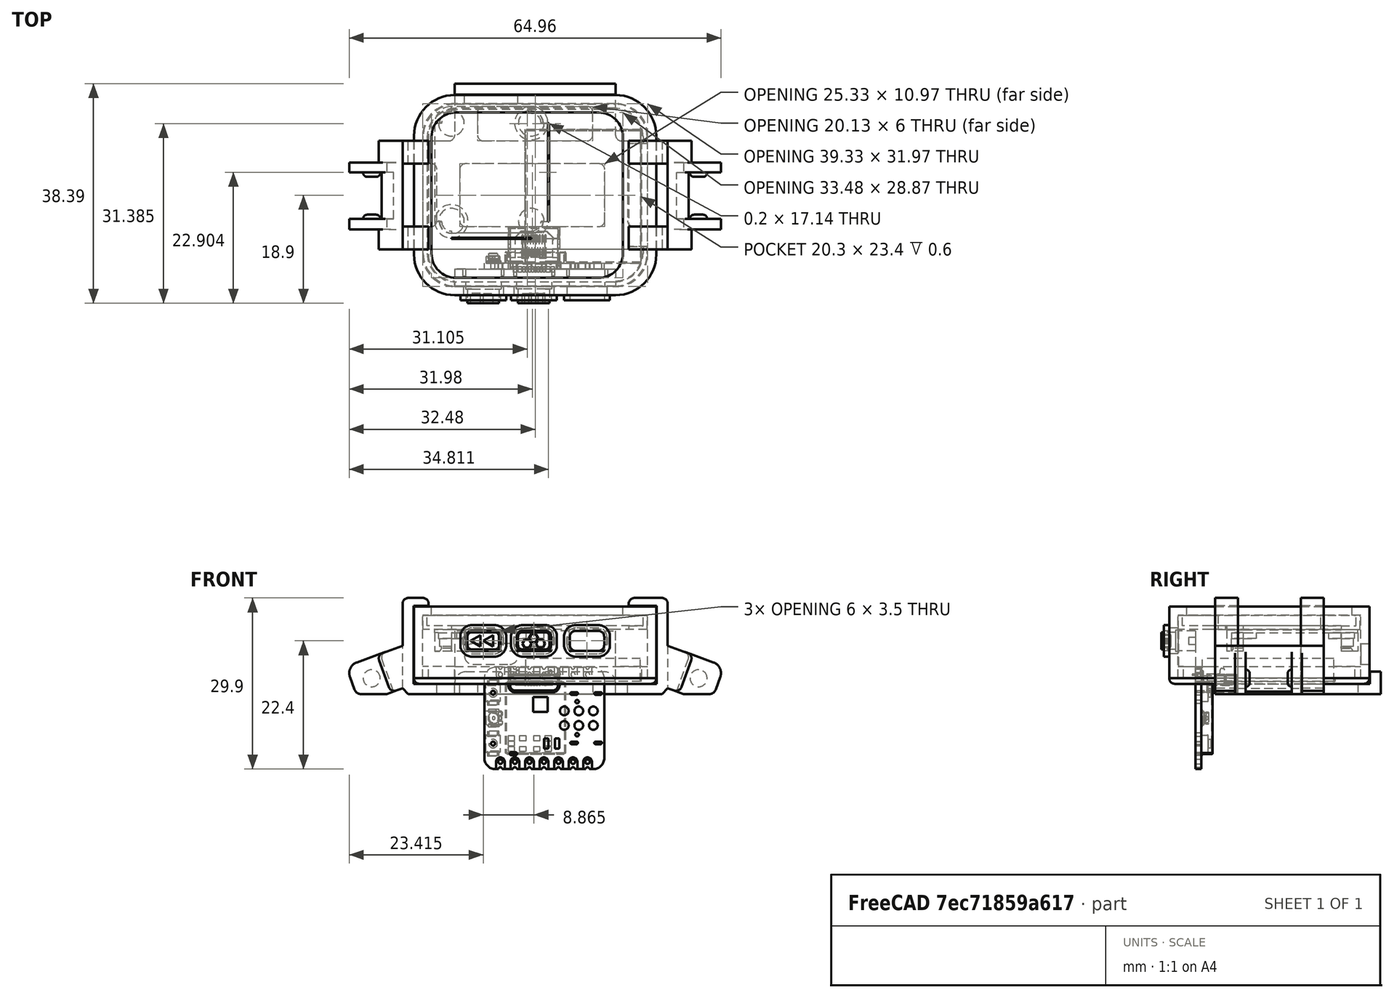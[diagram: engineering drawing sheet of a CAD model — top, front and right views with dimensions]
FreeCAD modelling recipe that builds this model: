
FCSTD DOCUMENT  (FreeCAD 1.0R39109 (Git))
Label: espwatch-final
License: All rights reserved
LicenseURL: https://en.wikipedia.org/wiki/All_rights_reserved
objects: Sketcher::SketchObject×41, Part::Feature×32, PartDesign::Pad×24, PartDesign::Pocket×17, PartDesign::Body×16, PartDesign::SubShapeBinder×15, PartDesign::Fillet×13, PartDesign::FeatureBase×8, App::Part×3, PartDesign::Thickness×2, PartDesign::Chamfer×2, Mesh::Feature×2, Part::Mirroring×1, Part::MultiFuse×1
note: 337 computed .brp shape members not serialized (recipe doc carries the construction recipe); baked Part::Feature solids carry a one-line shape summary decoded from their .brp

FEATURE [Sketcher::SketchObject] Sketch
  ArcFitTolerance = 1e-06
  AttachmentSupport = -> [XY_Plane]
  FullyConstrained = false
  MakeInternals = false
  MapMode = 5
  sketch-geometry (8):
    g0: LineSegment StartX=-15.185 StartY=13.865 StartZ=0 EndX=-15.185 EndY=-13.865 EndZ=0
    g1: LineSegment StartX=15.185 StartY=13.865 StartZ=0 EndX=15.185 EndY=-13.865 EndZ=0
    g2: LineSegment StartX=-10.185 StartY=18.865 StartZ=0 EndX=10.185 EndY=18.865 EndZ=0
    g3: LineSegment StartX=-10.185 StartY=-18.865 StartZ=0 EndX=10.185 EndY=-18.865 EndZ=0
    g4: ArcOfCircle CenterX=-10.185 CenterY=-13.865 CenterZ=0 NormalX=0 NormalY=0 NormalZ=1 AngleXU=0 Radius=5 StartAngle=3.14159 EndAngle=4.71239
    g5: ArcOfCircle CenterX=-10.185 CenterY=13.865 CenterZ=0 NormalX=0 NormalY=0 NormalZ=1 AngleXU=0 Radius=5.00002 StartAngle=1.5708 EndAngle=3.14159
    g6: ArcOfCircle CenterX=10.185 CenterY=13.865 CenterZ=0 NormalX=0 NormalY=0 NormalZ=1 AngleXU=0 Radius=5.00002 StartAngle=0 EndAngle=1.57079
    g7: ArcOfCircle CenterX=10.185 CenterY=-13.865 CenterZ=0 NormalX=0 NormalY=0 NormalZ=1 AngleXU=0 Radius=5.00002 StartAngle=4.71239 EndAngle=6.28318
  constraints (20):
    c: Vertical(g0)
    c: Vertical(g1)
    c: Horizontal(g2)
    c: Horizontal(g3)
    c: Coincident(g4,g0)
    c: Coincident(g4,g3)
    c: Coincident(g5,g2)
    c: Coincident(g5,g0)
    c: Coincident(g6,g2)
    c: Coincident(g6,g1)
    c: Coincident(g7,g1)
    c: Coincident(g7,g3)
    c: Equal(g0,g1)
    c: Equal(g3,g2)
    c: Radius(g4) = 5
    c: DistanceX(g0,g1) = 30.37
    c: DistanceY(g5,g6) = 0
    c: Equal(g5,g6)
    c: Equal(g7,g6)
    c: DistanceY(g3,g2) = 37.73
FEATURE [PartDesign::Pad] Pad
  Direction = (0,0,1)
  Length = 1.9
  Length2 = 10
  Profile = -> Sketch
  ReferenceAxis = -> Sketch [N_Axis]
  Refine = true
  Suppressed = false
  Type = 0
FEATURE [PartDesign::Thickness] Thickness
  Base = -> Pad [Face10]
  BaseFeature = -> Pad
  Intersection = false
  Join = 1
  Mode = 0
  Refine = true
  SupportTransform = false
  Suppressed = false
  Value = 0.7
FEATURE [Sketcher::SketchObject] Sketch001
  ArcFitTolerance = 1e-06
  AttachmentSupport = -> [XY_Plane]
  ExternalGeometry = -> [Thickness]
  FullyConstrained = true
  MakeInternals = false
  MapMode = 5
  sketch-geometry (4):
    g0: LineSegment StartX=-9 StartY=19.365 StartZ=0 EndX=-9 EndY=16.365 EndZ=0
    g1: LineSegment StartX=-9 StartY=16.365 StartZ=0 EndX=9 EndY=16.365 EndZ=0
    g2: LineSegment StartX=9 StartY=16.365 StartZ=0 EndX=9 EndY=19.365 EndZ=0
    g3: LineSegment StartX=9 StartY=19.365 StartZ=0 EndX=-9 EndY=19.365 EndZ=0
  constraints (12):
    c: Coincident(g0,g1)
    c: Coincident(g1,g2)
    c: Coincident(g2,g3)
    c: Coincident(g3,g0)
    c: Vertical(g0)
    c: Vertical(g2)
    c: Horizontal(g1)
    c: Horizontal(g3)
    c: DistanceY(g0,g0) = 3
    c: DistanceX(g3,g3) = 18
    c: DistanceY(g0,g-3) = -0.5
    c: DistanceX(g-1,g1) = 9
FEATURE [PartDesign::Pocket] Pocket
  BaseFeature = -> Thickness
  Direction = (0,0,-1)
  Length = 1
  Length2 = 5
  Profile = -> Sketch001
  ReferenceAxis = -> Sketch001 [N_Axis]
  Refine = true
  Reversed = true
  Suppressed = false
  Type = 4
FEATURE [Sketcher::SketchObject] Sketch002
  ArcFitTolerance = 1e-06
  AttachmentSupport = -> [XY_Plane]
  FullyConstrained = false
  MakeInternals = false
  MapMode = 5
  sketch-geometry (4):
    g0: LineSegment StartX=-25.2734 StartY=26.0356 StartZ=0 EndX=-25.2734 EndY=-23.7351 EndZ=0
    g1: LineSegment StartX=-25.2734 StartY=-23.7351 StartZ=0 EndX=24.3747 EndY=-23.7351 EndZ=0
    g2: LineSegment StartX=24.3747 StartY=-23.7351 StartZ=0 EndX=24.3747 EndY=26.0356 EndZ=0
    g3: LineSegment StartX=24.3747 StartY=26.0356 StartZ=0 EndX=-25.2734 EndY=26.0356 EndZ=0
  constraints (8):
    c: Coincident(g0,g1)
    c: Coincident(g1,g2)
    c: Coincident(g2,g3)
    c: Coincident(g3,g0)
    c: Vertical(g0)
    c: Vertical(g2)
    c: Horizontal(g1)
    c: Horizontal(g3)
FEATURE [PartDesign::Pocket] Pocket001
  BaseFeature = -> Pocket
  Direction = (0,0,-1)
  Length = 2
  Length2 = -0.6
  Profile = -> Sketch002
  ReferenceAxis = -> Sketch002 [N_Axis]
  Refine = true
  Suppressed = false
  Type = 4
FEATURE [Sketcher::SketchObject] Sketch003
  ArcFitTolerance = 1e-06
  AttachmentSupport = -> [XY_Plane001]
  FullyConstrained = true
  MakeInternals = false
  MapMode = 5
  sketch-geometry (4):
    g0: LineSegment StartX=20 StartY=23 StartZ=0 EndX=20 EndY=0 EndZ=0
    g1: LineSegment StartX=20 StartY=0 StartZ=0 EndX=0 EndY=0 EndZ=0
    g2: LineSegment StartX=0 StartY=0 StartZ=0 EndX=0 EndY=23 EndZ=0
    g3: LineSegment StartX=0 StartY=23 StartZ=0 EndX=20 EndY=23 EndZ=0
  constraints (11):
    c: Coincident(g0,g1)
    c: Coincident(g1,g2)
    c: Coincident(g2,g3)
    c: Coincident(g3,g0)
    c: Vertical(g0)
    c: Vertical(g2)
    c: Horizontal(g1)
    c: Horizontal(g3)
    c: Coincident(g1,g-1)
    c: DistanceY(g0,g0) = 23
    c: DistanceX(g3,g3) = 20
FEATURE [PartDesign::Pad] Pad001
  Direction = (0,0,1)
  Length = 4
  Length2 = 10
  Profile = -> Sketch003
  ReferenceAxis = -> Sketch003 [N_Axis]
  Refine = true
  Suppressed = false
  Type = 0
FEATURE [PartDesign::Body] Body001  label="battery"
  AllowCompound = false
  Group = -> [Sketch003,Pad001]
  Origin = -> Origin001
  Placement = pos=(-1.3,1.2,1.1) rot=(0,0,1;0rad)
  Tip = -> Pad001
FEATURE [Part::Feature] Part__Feature  label="BOSS-EXTRUDE14_8_"
  shape: bbox 0.6 x 1 x 0.3 mm, 6 faces (baked)
FEATURE [Part::Feature] Part__Feature001  label="BOSS-EXTRUDE7_4_"
  shape: bbox 0.3 x 3.784 x 0.75 mm, 6 faces (baked)
FEATURE [Part::Feature] Part__Feature002  label="BOSS-EXTRUDE7_3_"
  shape: bbox 0.3 x 3.784 x 0.75 mm, 6 faces (baked)
FEATURE [Part::Feature] Part__Feature003  label="BOSS-EXTRUDE14_4_"
  shape: bbox 0.3 x 1 x 0.3 mm, 6 faces (baked)
FEATURE [Part::Feature] Part__Feature004  label="BOSS-EXTRUDE14_2_"
  shape: bbox 0.6 x 1 x 0.3 mm, 6 faces (baked)
FEATURE [Part::Feature] Part__Feature005  label="BOSS-EXTRUDE14_11_"
  shape: bbox 0.3 x 1 x 0.3 mm, 6 faces (baked)
FEATURE [Part::Feature] Part__Feature006  label="BOSS-EXTRUDE7_7_"
  shape: bbox 0.3 x 3.784 x 0.75 mm, 6 faces (baked)
FEATURE [Part::Feature] Part__Feature007  label="BOSS-EXTRUDE14_9_"
  shape: bbox 0.3 x 1 x 0.3 mm, 6 faces (baked)
FEATURE [Part::Feature] Part__Feature008  label="BOSS-EXTRUDE14_3_"
  shape: bbox 0.3 x 1 x 0.3 mm, 6 faces (baked)
FEATURE [Part::Feature] Part__Feature009  label="BOSS-EXTRUDE14_7_"
  shape: bbox 0.6 x 1 x 0.3 mm, 6 faces (baked)
FEATURE [Part::Feature] Part__Feature010  label="MIRROR2"
  shape: bbox 6.7 x 4.6 x 0.7 mm, 26 faces (baked)
FEATURE [Part::Feature] Part__Feature011  label="BOSS-EXTRUDE14_5_"
  shape: bbox 0.3 x 1 x 0.3 mm, 6 faces (baked)
FEATURE [Part::Feature] Part__Feature012  label="BOSS-EXTRUDE14_12_"
  shape: bbox 0.3 x 1 x 0.3 mm, 6 faces (baked)
FEATURE [Part::Feature] Part__Feature013  label="BOSS-EXTRUDE7_8_"
  shape: bbox 0.3 x 3.784 x 0.75 mm, 6 faces (baked)
FEATURE [Part::Feature] Part__Feature014  label="BOSS-EXTRUDE7_1_"
  shape: bbox 0.3 x 3.784 x 0.75 mm, 6 faces (baked)
FEATURE [Part::Feature] Part__Feature015  label="BOSS-EXTRUDE14_10_"
  shape: bbox 0.3 x 1 x 0.3 mm, 6 faces (baked)
FEATURE [Part::Feature] Part__Feature016  label="BOSS-EXTRUDE7_9_"
  shape: bbox 0.3 x 3.784 x 0.75 mm, 6 faces (baked)
FEATURE [Part::Feature] Part__Feature017  label="BOSS-EXTRUDE14_6_"
  shape: bbox 0.6 x 1 x 0.3 mm, 6 faces (baked)
FEATURE [Part::Feature] Part__Feature018  label="CHAMFER9"
  shape: bbox 8.94 x 7.3 x 4.2 mm, 103 faces (baked)
FEATURE [Part::Feature] Part__Feature019  label="BOSS-EXTRUDE14_1_"
  shape: bbox 0.3 x 1 x 0.3 mm, 6 faces (baked)
FEATURE [Part::Feature] Part__Feature020  label="BOSS-EXTRUDE7_6_"
  shape: bbox 0.3 x 3.784 x 0.75 mm, 6 faces (baked)
FEATURE [Part::Feature] Part__Feature021  label="BOSS-EXTRUDE7_2_"
  shape: bbox 0.3 x 3.784 x 0.75 mm, 6 faces (baked)
FEATURE [Part::Feature] Part__Feature022  label="CUT-EXTRUDE5"
  shape: bbox 8.867 x 2 x 3.668 mm, 129 faces (baked)
FEATURE [Part::Feature] Part__Feature023  label="BOSS-EXTRUDE7_5_"
  shape: bbox 0.3 x 3.784 x 0.75 mm, 6 faces (baked)
FEATURE [App::Part] USB_TYPE_C_PORT__1_  label="USB TYPE C PORT (1)"
  Group = -> [Part__Feature,Part__Feature001,Part__Feature002,Part__Feature003,Part__Feature004,Part__Feature005,Part__Feature006,Part__Feature007,Part__Feature008,Part__Feature009,Part__Feature010,Part__Feature011,Part__Feature012,Part__Feature013,Part__Feature014,Part__Feature015,Part__Feature016,Part__Feature017,Part__Feature018,Part__Feature019,Part__Feature020,Part__Feature021,Part__Feature022,+1 more]
  Origin = -> Origin002
  Placement = pos=(0,0,-1e-16) rot=(0,0,1;0rad)
FEATURE [App::Part] USB_TYPE_C_PORT  label="USB TYPE C PORT"
  Group = -> [USB_TYPE_C_PORT__1_]
  Origin = -> Origin003
  Placement = pos=(6.48966,2.605,-6.1114) rot=(0.57735,0.57735,-0.57735;2.0944rad)
FEATURE [Part::Feature] Part__Feature024  label="U.FL Connector v1"
  Placement = pos=(-7.04101,1,-6.10146) rot=(0,-1,0;1.5708rad)
  shape: bbox 2.6 x 1.3 x 3 mm, 54 faces, 3 solids (baked)
FEATURE [Part::Feature] Part__Feature025  label="Button (1)"
  shape: bbox 2.5 x 1.7 x 4.303 mm, 19 faces (baked)
FEATURE [Part::Feature] Part__Feature026  label="Shield"
  shape: bbox 10.6 x 2.7 x 12.6 mm, 38 faces (baked)
FEATURE [Part::Feature] Part__Feature027  label="Button (1)001"
  Placement = pos=(-3.73e-13,1.1e-15,8.89) rot=(0,0,1;0rad)
  shape: bbox 2.5 x 1.7 x 4.303 mm, 19 faces (baked)
FEATURE [Part::Feature] Part__Feature028  label="SOLID"
  shape: bbox 20.96 x 1 x 17.78 mm, 358 faces (baked)
FEATURE [App::Part] Seeed_Studio_XIAO_ESP32_C3_v15  label="Seeed Studio XIAO-ESP32-C3 v15"
  Group = -> [USB_TYPE_C_PORT,Part__Feature024,Part__Feature025,Part__Feature026,Part__Feature027,Part__Feature028]
  Origin = -> Origin004
  Placement = pos=(-13.57,15.1,7.7) rot=(0.57735,0.57735,-0.57735;4.18879rad)
FEATURE [Sketcher::SketchObject] Sketch011
  ArcFitTolerance = 1e-06
  AttachmentSupport = -> [XY_Plane]
  ExternalGeometry = -> [Pocket001]
  FullyConstrained = true
  MakeInternals = false
  MapMode = 5
  sketch-geometry (4):
    g0: LineSegment StartX=-9 StartY=18.865 StartZ=0 EndX=9 EndY=18.865 EndZ=0
    g1: LineSegment StartX=9 StartY=18.865 StartZ=0 EndX=9 EndY=19.665 EndZ=0
    g2: LineSegment StartX=9 StartY=19.665 StartZ=0 EndX=-9 EndY=19.665 EndZ=0
    g3: LineSegment StartX=-9 StartY=19.665 StartZ=0 EndX=-9 EndY=18.865 EndZ=0
  constraints (11):
    c: Coincident(g0,g1)
    c: Coincident(g1,g2)
    c: Coincident(g2,g3)
    c: Coincident(g3,g0)
    c: Horizontal(g0)
    c: Horizontal(g2)
    c: Vertical(g1)
    c: Vertical(g3)
    c: Coincident(g0,g-3)
    c: DistanceX(g0,g-3) = 0
    c: DistanceY(g1,g1) = 0.8
FEATURE [PartDesign::Pocket] Pocket005
  BaseFeature = -> Pocket001
  Direction = (0,0,-1)
  Length = 5
  Length2 = 5
  Midplane = true
  Profile = -> Sketch011
  ReferenceAxis = -> Sketch011 [N_Axis]
  Refine = true
  Suppressed = false
  Type = 0
FEATURE [PartDesign::SubShapeBinder] Binder
  BindCopyOnChange = 0
  BindMode = 0
  ClaimChildren = false
  Context = -> Body002 [Binder.]
  Fuse = false
  MakeFace = true
  OffsetFill = false
  OffsetIntersection = false
  OffsetJoinType = 0
  OffsetOpenResult = false
  PartialLoad = false
  Refine = true
  Relative = true
  Support = -> [Body[Pocket005.,Pocket005.]]
  _Version = 2
FEATURE [Sketcher::SketchObject] Sketch012
  ArcFitTolerance = 1e-06
  AttachmentSupport = -> [XY_Plane005]
  FullyConstrained = true
  MakeInternals = false
  MapMode = 5
  sketch-geometry (10):
    g0: LineSegment StartX=-19.465 StartY=23.285 StartZ=0 EndX=-19.465 EndY=2.51502 EndZ=0
    g1: LineSegment StartX=-13.865 StartY=-3.085 StartZ=0 EndX=14.265 EndY=-3.085 EndZ=0
    g2: LineSegment StartX=19.865 StartY=2.51502 StartZ=0 EndX=19.865 EndY=23.285 EndZ=0
    g3: LineSegment StartX=14.265 StartY=28.885 StartZ=0 EndX=-13.865 EndY=28.885 EndZ=0
    g4: ArcOfCircle CenterX=-13.865 CenterY=23.285 CenterZ=0 NormalX=0 NormalY=0 NormalZ=1 AngleXU=0 Radius=5.60002 StartAngle=1.5708 EndAngle=3.14159
    g5: ArcOfCircle CenterX=-13.865 CenterY=2.51502 CenterZ=0 NormalX=0 NormalY=0 NormalZ=1 AngleXU=0 Radius=5.60002 StartAngle=3.14159 EndAngle=4.71239
    g6: ArcOfCircle CenterX=14.265 CenterY=2.51502 CenterZ=0 NormalX=0 NormalY=0 NormalZ=1 AngleXU=0 Radius=5.60002 StartAngle=4.71239 EndAngle=6.28319
    g7: ArcOfCircle CenterX=14.265 CenterY=23.285 CenterZ=0 NormalX=0 NormalY=0 NormalZ=1 AngleXU=0 Radius=5.60002 StartAngle=2e-16 EndAngle=1.5708
    g8: GeomPoint [constr] X=-19.465 Y=28.885 Z=0
    g9: GeomPoint [constr] X=19.865 Y=-3.085 Z=0
  constraints (24):
    c: Tangent(g0,g4) = -1.5708
    c: Tangent(g0,g5) = -1.5708
    c: Tangent(g1,g5) = -1.5708
    c: Tangent(g1,g6) = -1.5708
    c: Tangent(g2,g6) = -1.5708
    c: Tangent(g2,g7) = -1.5708
    c: Tangent(g3,g7) = -1.5708
    c: Tangent(g3,g4) = -1.5708
    c: Vertical(g0)
    c: Vertical(g2)
    c: Horizontal(g1)
    c: Horizontal(g3)
    c: Equal(g4,g5)
    c: Equal(g5,g6)
    c: Equal(g6,g7)
    c: PointOnObject(g8,g0)
    c: PointOnObject(g8,g3)
    c: PointOnObject(g9,g1)
    c: PointOnObject(g9,g2)
    c: Equal(g-5,g5)
    c: DistanceX(g0,g-7) = 0.2
    c: DistanceX(g-6,g2) = 0.2
    c: DistanceY(g-3,g3) = 0.2
    c: DistanceY(g1,g-4) = 0.2
FEATURE [PartDesign::Pad] Pad002
  Direction = (0,0,1)
  Length = 11
  Length2 = 10
  Profile = -> Sketch012
  ReferenceAxis = -> Sketch012 [N_Axis]
  Refine = true
  Suppressed = false
  Type = 0
FEATURE [PartDesign::Thickness] Thickness001
  Base = -> Pad002 [Face9]
  BaseFeature = -> Pad002
  Intersection = false
  Join = 1
  Mode = 0
  Refine = true
  SupportTransform = false
  Suppressed = false
  Value = 1.5
FEATURE [PartDesign::SubShapeBinder] Binder001
  BindCopyOnChange = 0
  BindMode = 0
  ClaimChildren = false
  Context = -> Body002 [Binder001.]
  Fuse = false
  MakeFace = true
  OffsetFill = false
  OffsetIntersection = false
  OffsetJoinType = 0
  OffsetOpenResult = false
  PartialLoad = false
  Refine = true
  Relative = true
  Support = -> [Body[Pocket005.Edge10,Pocket005.Edge21,Pocket005.Edge20,Pocket005.Edge23,Pocket005.Edge25,Pocket005.Edge7]]
  _Version = 2
FEATURE [Sketcher::SketchObject] Sketch013
  ArcFitTolerance = 1e-06
  AttachmentSupport = -> [XY_Plane005]
  ExternalGeometry = -> [Binder001]
  FullyConstrained = true
  MakeInternals = false
  MapMode = 5
  sketch-geometry (10):
    g0: LineSegment StartX=-13.665 StartY=-1.535 StartZ=0 EndX=11.315 EndY=-1.535 EndZ=0
    g1: LineSegment StartX=15.565 StartY=2.715 StartZ=0 EndX=15.565 EndY=23.085 EndZ=0
    g2: LineSegment StartX=11.315 StartY=27.335 StartZ=0 EndX=-13.665 EndY=27.335 EndZ=0
    g3: LineSegment StartX=-17.915 StartY=23.085 StartZ=0 EndX=-17.915 EndY=2.715 EndZ=0
    g4: ArcOfCircle CenterX=-13.665 CenterY=2.715 CenterZ=0 NormalX=0 NormalY=0 NormalZ=1 AngleXU=0 Radius=4.25 StartAngle=3.14159 EndAngle=4.71239
    g5: ArcOfCircle CenterX=11.315 CenterY=2.715 CenterZ=0 NormalX=0 NormalY=0 NormalZ=1 AngleXU=0 Radius=4.25 StartAngle=4.71239 EndAngle=6.28319
    g6: ArcOfCircle CenterX=11.315 CenterY=23.085 CenterZ=0 NormalX=0 NormalY=0 NormalZ=1 AngleXU=0 Radius=4.25 StartAngle=3e-16 EndAngle=1.5708
    g7: ArcOfCircle CenterX=-13.665 CenterY=23.085 CenterZ=0 NormalX=0 NormalY=0 NormalZ=1 AngleXU=0 Radius=4.25 StartAngle=1.5708 EndAngle=3.14159
    g8: GeomPoint [constr] X=-17.915 Y=-1.535 Z=0
    g9: GeomPoint [constr] X=15.565 Y=27.335 Z=0
  constraints (24):
    c: Tangent(g0,g4) = -1.5708
    c: Tangent(g0,g5) = -1.5708
    c: Tangent(g1,g5) = -1.5708
    c: Tangent(g1,g6) = -1.5708
    c: Tangent(g2,g6) = -1.5708
    c: Tangent(g2,g7) = -1.5708
    c: Tangent(g3,g7) = -1.5708
    c: Tangent(g3,g4) = -1.5708
    c: Horizontal(g0)
    c: Horizontal(g2)
    c: Vertical(g1)
    c: Vertical(g3)
    c: Equal(g4,g5)
    c: Equal(g5,g6)
    c: Equal(g6,g7)
    c: PointOnObject(g8,g0)
    c: PointOnObject(g8,g3)
    c: PointOnObject(g9,g1)
    c: PointOnObject(g9,g2)
    c: DistanceX(g-4,g3) = 0.75
    c: DistanceY(g-3,g0) = 0.75
    c: DistanceY(g2,g-6) = 0.75
    c: DistanceX(g1,g-7) = 3.5
    c: DistanceY(g3,g-6) = 0
FEATURE [PartDesign::Pocket] Pocket006
  BaseFeature = -> Thickness001
  Direction = (0,0,-1)
  Length = 20
  Length2 = 5
  Profile = -> Sketch013
  ReferenceAxis = -> Sketch013 [N_Axis]
  Refine = true
  Reversed = true
  Suppressed = false
  Type = 0
FEATURE [PartDesign::SubShapeBinder] Binder002
  BindCopyOnChange = 0
  BindMode = 0
  ClaimChildren = false
  Context = -> Body003 [Binder002.]
  Fuse = false
  MakeFace = true
  OffsetFill = false
  OffsetIntersection = false
  OffsetJoinType = 0
  OffsetOpenResult = false
  PartialLoad = false
  Refine = true
  Relative = true
  Support = -> [Seeed_Studio_XIAO_ESP32_C3_v15[Part__Feature028.Edge47,Part__Feature028.Edge45,Part__Feature028.Edge15,Part__Feature028.Edge13]]
  _Version = 2
FEATURE [Sketcher::SketchObject] Sketch015
  ArcFitTolerance = 1e-06
  AttachmentSupport = -> [XY_Plane006]
  ExternalGeometry = -> [Binder002]
  FullyConstrained = true
  MakeInternals = false
  MapMode = 5
  sketch-geometry (10):
    g0: LineSegment StartX=-14.4436 StartY=5.42666 StartZ=0 EndX=-0.473644 EndY=5.42666 EndZ=0
    g1: LineSegment StartX=2.4314 StartY=8.3317 StartZ=0 EndX=2.4314 EndY=25.4766 EndZ=0
    g2: LineSegment StartX=-0.473644 StartY=28.3817 StartZ=0 EndX=-14.4436 EndY=28.3817 EndZ=0
    g3: LineSegment StartX=-17.3486 StartY=25.4766 StartZ=0 EndX=-17.3486 EndY=8.3317 EndZ=0
    g4: ArcOfCircle CenterX=-14.4436 CenterY=8.3317 CenterZ=0 NormalX=0 NormalY=0 NormalZ=1 AngleXU=0 Radius=2.90504 StartAngle=3.14159 EndAngle=4.71239
    g5: ArcOfCircle CenterX=-0.473644 CenterY=8.3317 CenterZ=0 NormalX=0 NormalY=0 NormalZ=1 AngleXU=0 Radius=2.90504 StartAngle=4.71239 EndAngle=6.28319
    g6: ArcOfCircle CenterX=-0.473644 CenterY=25.4766 CenterZ=0 NormalX=0 NormalY=0 NormalZ=1 AngleXU=0 Radius=2.90504 StartAngle=0 EndAngle=1.5708
    g7: ArcOfCircle CenterX=-14.4436 CenterY=25.4766 CenterZ=0 NormalX=0 NormalY=0 NormalZ=1 AngleXU=0 Radius=2.90504 StartAngle=1.5708 EndAngle=3.14159
    g8: GeomPoint [constr] X=-17.3486 Y=5.42666 Z=0
    g9: GeomPoint [constr] X=2.4314 Y=28.3817 Z=0
  constraints (22):
    c: Tangent(g0,g4) = -1.5708
    c: Tangent(g0,g5) = -1.5708
    c: Tangent(g1,g5) = -1.5708
    c: Tangent(g1,g6) = -1.5708
    c: Tangent(g2,g6) = -1.5708
    c: Tangent(g2,g7) = -1.5708
    c: Tangent(g3,g7) = -1.5708
    c: Tangent(g3,g4) = -1.5708
    c: Horizontal(g0)
    c: Horizontal(g2)
    c: Vertical(g1)
    c: Vertical(g3)
    c: Equal(g4,g5)
    c: Equal(g5,g6)
    c: Equal(g6,g7)
    c: PointOnObject(g8,g0)
    c: PointOnObject(g8,g3)
    c: PointOnObject(g9,g1)
    c: PointOnObject(g9,g2)
    c: Coincident(g6,g-3)
    c: Coincident(g4,g-5)
    c: DistanceY(g0,g-6) = 1
FEATURE [PartDesign::Pad] Pad003
  Direction = (0,0,1)
  Length = 9.5
  Length2 = -9
  Profile = -> Sketch015
  ReferenceAxis = -> Sketch015 [N_Axis]
  Refine = true
  Suppressed = false
  Type = 4
FEATURE [Sketcher::SketchObject] Sketch014
  ArcFitTolerance = 1e-06
  AttachmentSupport = -> [XY_Plane006]
  ExternalGeometry = -> [Binder002,Pad003]
  FullyConstrained = true
  MakeInternals = false
  MapMode = 5
  sketch-geometry (16):
    g0: ArcOfCircle CenterX=-14.4436 CenterY=25.4766 CenterZ=0 NormalX=0 NormalY=0 NormalZ=1 AngleXU=0 Radius=2.90504 StartAngle=1.57081 EndAngle=3.14159
    g1: ArcOfCircle CenterX=-14.4436 CenterY=25.4766 CenterZ=0 NormalX=0 NormalY=0 NormalZ=1 AngleXU=0 Radius=2.10504 StartAngle=1.57082 EndAngle=3.14157
    g2: LineSegment StartX=-16.5486 StartY=25.4767 StartZ=0 EndX=-17.3486 EndY=25.4766 EndZ=0
    g3: LineSegment StartX=-14.4436 StartY=27.5817 StartZ=0 EndX=-14.4436 EndY=28.3817 EndZ=0
    g4: ArcOfCircle CenterX=-0.473644 CenterY=25.4766 CenterZ=0 NormalX=0 NormalY=0 NormalZ=1 AngleXU=0 Radius=2.90504 StartAngle=0 EndAngle=1.57078
    g5: ArcOfCircle CenterX=-14.4436 CenterY=8.3317 CenterZ=0 NormalX=0 NormalY=0 NormalZ=1 AngleXU=0 Radius=2.90504 StartAngle=3.14161 EndAngle=4.71239
    g6: ArcOfCircle CenterX=-0.473644 CenterY=8.3317 CenterZ=0 NormalX=0 NormalY=0 NormalZ=1 AngleXU=0 Radius=2.90504 StartAngle=4.71239 EndAngle=6.28319
    g7: ArcOfCircle CenterX=-14.4436 CenterY=8.3317 CenterZ=0 NormalX=0 NormalY=0 NormalZ=1 AngleXU=0 Radius=2.10504 StartAngle=3.14161 EndAngle=4.71239
    g8: ArcOfCircle CenterX=-0.473644 CenterY=8.3317 CenterZ=0 NormalX=0 NormalY=0 NormalZ=1 AngleXU=0 Radius=2.10504 StartAngle=4.71239 EndAngle=6.28319
    g9: ArcOfCircle CenterX=-0.473644 CenterY=25.4766 CenterZ=0 NormalX=0 NormalY=0 NormalZ=1 AngleXU=0 Radius=2.10504 StartAngle=0 EndAngle=1.57078
    g10: LineSegment StartX=-0.4736 StartY=28.3817 StartZ=0 EndX=-0.4736 EndY=27.5817 EndZ=0
    g11: LineSegment StartX=1.6314 StartY=25.4766 StartZ=0 EndX=2.4314 EndY=25.4766 EndZ=0
    g12: LineSegment StartX=-0.473644 StartY=6.22666 StartZ=0 EndX=-0.473644 EndY=5.42666 EndZ=0
    g13: LineSegment StartX=1.6314 StartY=8.3317 StartZ=0 EndX=2.4314 EndY=8.3317 EndZ=0
    g14: LineSegment StartX=-17.3486 StartY=8.33166 StartZ=0 EndX=-16.5486 EndY=8.33166 EndZ=0
    g15: LineSegment StartX=-14.4436 StartY=6.22666 StartZ=0 EndX=-14.4436 EndY=5.42666 EndZ=0
  constraints (45):
    c: Coincident(g0,g-10)
    c: Coincident(g0,g-10)
    c: Coincident(g1,g-10)
    c: DistanceY(g-5,g1) = 0
    c: DistanceX(g-5,g1) = 0
    c: DistanceY(g-5,g1) = 0.2
    c: Coincident(g3,g1)
    c: Coincident(g3,g0)
    c: Vertical(g3)
    c: Coincident(g2,g0)
    c: Coincident(g4,g-11)
    c: Coincident(g4,g-11)
    c: Coincident(g5,g-9)
    c: Coincident(g5,g-9)
    c: Coincident(g8,g6)
    c: Coincident(g9,g-11)
    c: DistanceX(g-7,g9) = 0.2
    c: Coincident(g10,g4)
    c: Coincident(g10,g9)
    c: DistanceX(g9,g-7) = 0
    c: Parallel(g10,g-2)
    c: Coincident(g9,g11)
    c: Coincident(g4,g11)
    c: Perpendicular(g-2,g11)
    c: Coincident(g12,g8)
    c: Coincident(g12,g6)
    c: Coincident(g13,g8)
    c: Coincident(g13,g6)
    c: Horizontal(g13)
    c: Parallel(g12,g-2)
    c: Coincident(g6,g-8)
    c: Coincident(g6,g-8)
    c: DistanceX(g-3,g8) = 0.2
    c: DistanceY(g6,g-8) = 0
    c: Coincident(g14,g5)
    c: Coincident(g14,g7)
    c: Coincident(g15,g7)
    c: Coincident(g15,g5)
    c: Vertical(g15)
    c: Perpendicular(g-2,g14)
    c: DistanceX(g7,g-4) = 0.2
    c: DistanceY(g7,g5) = 0
    c: DistanceX(g5,g7) = 0
    c: Coincident(g2,g1)
    c: DistanceY(g-4,g7) = 0
FEATURE [PartDesign::Pad] Pad004
  BaseFeature = -> Pad003
  Direction = (0,0,1)
  Length = 5.8
  Length2 = -9.4
  Profile = -> Sketch014
  ReferenceAxis = -> Sketch014 [N_Axis]
  Refine = true
  Suppressed = false
  Type = 4
FEATURE [Sketcher::SketchObject] Sketch016
  ArcFitTolerance = 1e-06
  AttachmentSupport = -> [XY_Plane006]
  ExternalGeometry = -> [Binder002]
  FullyConstrained = true
  MakeInternals = false
  MapMode = 5
  sketch-geometry (4):
    g0: Circle CenterX=-14.4436 CenterY=8.3317 CenterZ=0 NormalX=0 NormalY=0 NormalZ=1 AngleXU=0 Radius=2.25
    g1: Circle CenterX=-0.473644 CenterY=8.3317 CenterZ=0 NormalX=0 NormalY=0 NormalZ=1 AngleXU=0 Radius=2.25
    g2: Circle CenterX=-0.473644 CenterY=25.4766 CenterZ=0 NormalX=0 NormalY=0 NormalZ=1 AngleXU=0 Radius=2.25
    g3: Circle CenterX=-14.4436 CenterY=25.4766 CenterZ=0 NormalX=0 NormalY=0 NormalZ=1 AngleXU=0 Radius=2.25
  constraints (9):
    c: Coincident(g0,g-4)
    c: Coincident(g1,g-3)
    c: Coincident(g2,g-6)
    c: Coincident(g3,g-5)
    c: Equal(g3,g0)
    c: Equal(g0,g1)
    c: Equal(g1,g2)
    c: Radius(g-6) = 1.90504
    c: Diameter(g2) = 4.5
FEATURE [PartDesign::Pad] Pad005
  BaseFeature = -> Pad004
  Direction = (0,0,1)
  Length = 9.4
  Length2 = -8
  Profile = -> Sketch016
  ReferenceAxis = -> Sketch016 [N_Axis]
  Refine = true
  Suppressed = false
  Type = 4
FEATURE [PartDesign::SubShapeBinder] Binder003
  BindCopyOnChange = 0
  BindMode = 0
  ClaimChildren = false
  Context = -> Body003 [Binder003.]
  Fuse = false
  MakeFace = true
  OffsetFill = false
  OffsetIntersection = false
  OffsetJoinType = 0
  OffsetOpenResult = false
  PartialLoad = false
  Refine = true
  Relative = true
  Support = -> [Pad005[Edge7,Edge44,Edge14,Edge55,Edge72,Edge93,Edge89,Edge84]]
  _Version = 2
FEATURE [Sketcher::SketchObject] Sketch017
  ArcFitTolerance = 1e-06
  AttachmentSupport = -> [XY_Plane006]
  ExternalGeometry = -> [Binder003]
  FullyConstrained = true
  MakeInternals = false
  MapMode = 5
  sketch-geometry (16):
    g0: ArcOfCircle CenterX=-14.4436 CenterY=8.3317 CenterZ=0 NormalX=0 NormalY=0 NormalZ=1 AngleXU=0 Radius=2.90504 StartAngle=3.14161 EndAngle=4.71239
    g1: ArcOfCircle CenterX=-0.473644 CenterY=8.3317 CenterZ=0 NormalX=0 NormalY=0 NormalZ=1 AngleXU=0 Radius=2.90504 StartAngle=4.71239 EndAngle=6.28319
    g2: ArcOfCircle CenterX=-0.473644 CenterY=25.4766 CenterZ=0 NormalX=0 NormalY=0 NormalZ=1 AngleXU=0 Radius=2.90504 StartAngle=3e-16 EndAngle=1.57078
    g3: ArcOfCircle CenterX=-14.4436 CenterY=25.4766 CenterZ=0 NormalX=0 NormalY=0 NormalZ=1 AngleXU=0 Radius=2.90504 StartAngle=1.57081 EndAngle=3.14159
    g4: ArcOfCircle CenterX=-14.4436 CenterY=8.3317 CenterZ=0 NormalX=0 NormalY=0 NormalZ=1 AngleXU=0 Radius=1.70504 StartAngle=3.14162 EndAngle=4.71239
    g5: ArcOfCircle CenterX=-14.4436 CenterY=25.4766 CenterZ=0 NormalX=0 NormalY=0 NormalZ=1 AngleXU=0 Radius=1.70504 StartAngle=1.57082 EndAngle=3.14157
    g6: ArcOfCircle CenterX=-0.473644 CenterY=25.4766 CenterZ=0 NormalX=0 NormalY=0 NormalZ=1 AngleXU=0 Radius=1.70504 StartAngle=2e-16 EndAngle=1.57077
    g7: ArcOfCircle CenterX=-0.473644 CenterY=8.3317 CenterZ=0 NormalX=0 NormalY=0 NormalZ=1 AngleXU=0 Radius=1.70504 StartAngle=4.71239 EndAngle=6.28319
    g8: LineSegment StartX=-14.4436 StartY=28.3817 StartZ=0 EndX=-14.4436 EndY=27.1817 EndZ=0
    g9: LineSegment StartX=-16.1486 StartY=25.4767 StartZ=0 EndX=-17.3486 EndY=25.4766 EndZ=0
    g10: LineSegment StartX=2.4314 StartY=25.4766 StartZ=0 EndX=1.2314 EndY=25.4766 EndZ=0
    g11: LineSegment StartX=-0.4736 StartY=28.3817 StartZ=0 EndX=-0.4736 EndY=27.1817 EndZ=0
    g12: LineSegment StartX=-14.4436 StartY=5.42666 StartZ=0 EndX=-14.4436 EndY=6.62666 EndZ=0
    g13: LineSegment StartX=-17.3486 StartY=8.33166 StartZ=0 EndX=-16.1486 EndY=8.33166 EndZ=0
    g14: LineSegment StartX=-0.473644 StartY=5.42666 StartZ=0 EndX=-0.473644 EndY=6.62666 EndZ=0
    g15: LineSegment StartX=2.4314 StartY=8.3317 StartZ=0 EndX=1.2314 EndY=8.3317 EndZ=0
  constraints (44):
    c: Coincident(g0,g-5)
    c: Coincident(g1,g-10)
    c: Coincident(g2,g-9)
    c: Coincident(g3,g-7)
    c: Coincident(g4,g0)
    c: Coincident(g5,g3)
    c: Coincident(g6,g2)
    c: Coincident(g7,g1)
    c: DistanceY(g-6,g5) = 0
    c: Coincident(g3,g-7)
    c: DistanceX(g3,g-7) = 0
    c: Coincident(g8,g3)
    c: Vertical(g8)
    c: Coincident(g5,g8)
    c: DistanceY(g5,g-6) = 0.4
    c: Coincident(g2,g-8)
    c: DistanceY(g-8,g2) = 0
    c: Coincident(g10,g2)
    c: Horizontal(g10)
    c: Coincident(g11,g2)
    c: Vertical(g11)
    c: Coincident(g6,g11)
    c: Coincident(g6,g10)
    c: DistanceX(g6,g-9) = 0.4
    c: Coincident(g0,g-5)
    c: DistanceX(g0,g-5) = 0
    c: Coincident(g12,g0)
    c: Coincident(g13,g0)
    c: Horizontal(g13)
    c: Parallel(g12,g-2)
    c: Coincident(g4,g13)
    c: Coincident(g4,g12)
    c: DistanceY(g-4,g4) = 0.4
    c: Coincident(g1,g-10)
    c: DistanceX(g1,g-10) = 0
    c: Coincident(g14,g1)
    c: Vertical(g14)
    c: Coincident(g15,g1)
    c: Horizontal(g15)
    c: Coincident(g15,g7)
    c: Coincident(g7,g14)
    c: DistanceY(g-3,g7) = 0.4
    c: Coincident(g9,g3)
    c: Coincident(g5,g9)
FEATURE [PartDesign::Pad] Pad006
  BaseFeature = -> Pad005
  Direction = (0,0,1)
  Length = 6.6
  Length2 = -5.8
  Profile = -> Sketch017
  ReferenceAxis = -> Sketch017 [N_Axis]
  Refine = true
  Suppressed = false
  Type = 4
FEATURE [PartDesign::Chamfer] Chamfer
  Angle = 35
  Base = -> Pad006 [Edge95,Edge92,Edge97,Edge100]
  BaseFeature = -> Pad006
  ChamferType = 2
  FlipDirection = false
  Refine = true
  Size = 0.5
  Size2 = 1
  SupportTransform = false
  Suppressed = false
  UseAllEdges = false
FEATURE [PartDesign::SubShapeBinder] Binder004
  BindCopyOnChange = 0
  BindMode = 0
  ClaimChildren = false
  Context = -> Body002 [Binder004.]
  Fuse = false
  MakeFace = true
  OffsetFill = false
  OffsetIntersection = false
  OffsetJoinType = 0
  OffsetOpenResult = false
  PartialLoad = false
  Refine = true
  Relative = true
  Support = -> <blob elided: 513 chars, md5=d62ed6e8>
  _Version = 2
FEATURE [Sketcher::SketchObject] Sketch018
  ArcFitTolerance = 1e-06
  AttachmentSupport = -> [XZ_Plane005]
  ExternalGeometry = -> [Binder004]
  FullyConstrained = true
  MakeInternals = false
  MapMode = 5
  Placement = pos=(0,0,0) rot=(1,0,0;1.5708rad)
  sketch-geometry (10):
    g0: LineSegment StartX=-10.6786 StartY=2.39 StartZ=0 EndX=-4.2386 EndY=2.39 EndZ=0
    g1: LineSegment StartX=-2.7886 StartY=3.84 StartZ=0 EndX=-2.7886 EndY=4.55 EndZ=0
    g2: LineSegment StartX=-4.2386 StartY=6 StartZ=0 EndX=-10.6786 EndY=6 EndZ=0
    g3: LineSegment StartX=-12.1286 StartY=4.55 StartZ=0 EndX=-12.1286 EndY=3.84 EndZ=0
    g4: ArcOfCircle CenterX=-10.6786 CenterY=3.84 CenterZ=0 NormalX=0 NormalY=0 NormalZ=1 AngleXU=0 Radius=1.45 StartAngle=3.14159 EndAngle=4.71239
    g5: ArcOfCircle CenterX=-4.2386 CenterY=3.84 CenterZ=0 NormalX=0 NormalY=0 NormalZ=1 AngleXU=0 Radius=1.45 StartAngle=4.71239 EndAngle=6.28319
    g6: ArcOfCircle CenterX=-4.2386 CenterY=4.55 CenterZ=0 NormalX=0 NormalY=0 NormalZ=1 AngleXU=0 Radius=1.45 StartAngle=0 EndAngle=1.5708
    g7: ArcOfCircle CenterX=-10.6786 CenterY=4.55 CenterZ=0 NormalX=0 NormalY=0 NormalZ=1 AngleXU=0 Radius=1.45 StartAngle=1.5708 EndAngle=3.14159
    g8: GeomPoint [constr] X=-12.1286 Y=2.39 Z=0
    g9: GeomPoint [constr] X=-2.7886 Y=6 Z=0
  constraints (21):
    c: Tangent(g0,g4) = -1.5708
    c: Tangent(g0,g5) = -1.5708
    c: Tangent(g1,g5) = -1.5708
    c: Tangent(g1,g6) = -1.5708
    c: Tangent(g2,g6) = -1.5708
    c: Tangent(g2,g7) = -1.5708
    c: Tangent(g3,g7) = -1.5708
    c: Tangent(g3,g4) = -1.5708
    c: Horizontal(g0)
    c: Horizontal(g2)
    c: Vertical(g1)
    c: Vertical(g3)
    c: Equal(g5,g6)
    c: PointOnObject(g8,g0)
    c: PointOnObject(g8,g3)
    c: PointOnObject(g9,g1)
    c: PointOnObject(g9,g2)
    c: Coincident(g4,g-4)
    c: Coincident(g7,g-5)
    c: Coincident(g-8,g5)
    c: DistanceY(g0,g-8) = 0.2
FEATURE [PartDesign::Pocket] Pocket007
  BaseFeature = -> Pocket006
  Direction = (0,1,-2e-16)
  Length = 32
  Length2 = 5
  Profile = -> Sketch018
  ReferenceAxis = -> Sketch018 [N_Axis]
  Refine = true
  Suppressed = false
  Type = 0
FEATURE [PartDesign::SubShapeBinder] Binder005
  BindCopyOnChange = 0
  BindMode = 0
  ClaimChildren = false
  Context = -> Body004 [Binder005.]
  Fuse = false
  MakeFace = true
  OffsetFill = false
  OffsetIntersection = false
  OffsetJoinType = 0
  OffsetOpenResult = false
  PartialLoad = false
  Refine = true
  Relative = true
  Support = -> [Body002[Pocket007.Face4]]
  _Version = 2
FEATURE [Sketcher::SketchObject] Sketch019
  ArcFitTolerance = 1e-06
  AttachmentSupport = -> [XY_Plane007]
  ExternalGeometry = -> [Binder005]
  FullyConstrained = true
  MakeInternals = false
  MapMode = 5
  sketch-geometry (20):
    g0: LineSegment StartX=-13.865 StartY=-3.085 StartZ=0 EndX=14.265 EndY=-3.085 EndZ=0
    g1: LineSegment StartX=19.865 StartY=2.51502 StartZ=0 EndX=19.865 EndY=23.285 EndZ=0
    g2: LineSegment StartX=14.265 StartY=28.885 StartZ=0 EndX=-13.865 EndY=28.885 EndZ=0
    g3: LineSegment StartX=-19.465 StartY=23.285 StartZ=0 EndX=-19.465 EndY=2.51502 EndZ=0
    g4: ArcOfCircle CenterX=-13.865 CenterY=2.51502 CenterZ=0 NormalX=0 NormalY=0 NormalZ=1 AngleXU=0 Radius=5.60002 StartAngle=3.14159 EndAngle=4.71239
    g5: ArcOfCircle CenterX=14.265 CenterY=2.51502 CenterZ=0 NormalX=0 NormalY=0 NormalZ=1 AngleXU=0 Radius=5.60002 StartAngle=4.71239 EndAngle=6.28319
    g6: ArcOfCircle CenterX=14.265 CenterY=23.285 CenterZ=0 NormalX=0 NormalY=0 NormalZ=1 AngleXU=0 Radius=5.60002 StartAngle=0 EndAngle=1.5708
    g7: ArcOfCircle CenterX=-13.865 CenterY=23.285 CenterZ=0 NormalX=0 NormalY=0 NormalZ=1 AngleXU=0 Radius=5.60002 StartAngle=1.5708 EndAngle=3.14159
    g8: GeomPoint [constr] X=-19.465 Y=-3.085 Z=0
    g9: GeomPoint [constr] X=19.865 Y=28.885 Z=0
    g10: LineSegment StartX=-18.465 StartY=23.285 StartZ=0 EndX=-18.465 EndY=2.51502 EndZ=0
    g11: LineSegment StartX=-13.865 StartY=-2.085 StartZ=0 EndX=14.265 EndY=-2.085 EndZ=0
    g12: LineSegment StartX=18.865 StartY=2.51502 StartZ=0 EndX=18.865 EndY=23.285 EndZ=0
    g13: LineSegment StartX=14.265 StartY=27.885 StartZ=0 EndX=-13.865 EndY=27.885 EndZ=0
    g14: ArcOfCircle CenterX=-13.865 CenterY=23.285 CenterZ=0 NormalX=0 NormalY=0 NormalZ=1 AngleXU=0 Radius=4.60002 StartAngle=1.5708 EndAngle=3.14159
    g15: ArcOfCircle CenterX=-13.865 CenterY=2.51502 CenterZ=0 NormalX=0 NormalY=0 NormalZ=1 AngleXU=0 Radius=4.60002 StartAngle=3.14159 EndAngle=4.71239
    g16: ArcOfCircle CenterX=14.265 CenterY=2.51502 CenterZ=0 NormalX=0 NormalY=0 NormalZ=1 AngleXU=0 Radius=4.60002 StartAngle=4.71239 EndAngle=6.28319
    g17: ArcOfCircle CenterX=14.265 CenterY=23.285 CenterZ=0 NormalX=0 NormalY=0 NormalZ=1 AngleXU=0 Radius=4.60002 StartAngle=0 EndAngle=1.5708
    g18: GeomPoint [constr] X=-18.465 Y=27.885 Z=0
    g19: GeomPoint [constr] X=18.865 Y=-2.085 Z=0
  constraints (46):
    c: Tangent(g0,g4) = -1.5708
    c: Tangent(g0,g5) = -1.5708
    c: Tangent(g1,g5) = -1.5708
    c: Tangent(g1,g6) = -1.5708
    c: Tangent(g2,g6) = -1.5708
    c: Tangent(g2,g7) = -1.5708
    c: Tangent(g3,g7) = -1.5708
    c: Tangent(g3,g4) = -1.5708
    c: Horizontal(g0)
    c: Horizontal(g2)
    c: Vertical(g3)
    c: Equal(g6,g7)
    c: PointOnObject(g8,g0)
    c: PointOnObject(g8,g3)
    c: PointOnObject(g9,g1)
    c: PointOnObject(g9,g2)
    c: Coincident(g0,g-7)
    c: Coincident(g1,g-7)
    c: DistanceX(g-3,g0) = 0
    c: DistanceY(g3,g-6) = 0
    c: DistanceX(g-4,g2) = 0
    c: DistanceY(g3,g-6) = 0
    c: Tangent(g10,g14) = -1.5708
    c: Tangent(g10,g15) = -1.5708
    c: Tangent(g11,g15) = -1.5708
    c: Tangent(g11,g16) = -1.5708
    c: Tangent(g12,g16) = -1.5708
    c: Tangent(g12,g17) = -1.5708
    c: Tangent(g13,g17) = -1.5708
    c: Tangent(g13,g14) = -1.5708
    c: Vertical(g10)
    c: Vertical(g12)
    c: Horizontal(g11)
    c: Horizontal(g13)
    c: Equal(g14,g15)
    c: Equal(g15,g16)
    c: Equal(g16,g17)
    c: PointOnObject(g18,g10)
    c: PointOnObject(g18,g13)
    c: PointOnObject(g19,g11)
    c: PointOnObject(g19,g12)
    c: DistanceY(g13,g2) = 1
    c: DistanceX(g13,g2) = 0
    c: DistanceY(g1,g12) = 0
    c: DistanceY(g1,g12) = 0
    c: DistanceX(g0,g11) = 0
FEATURE [PartDesign::Pad] Pad007
  Direction = (0,0,1)
  Length = 2
  Length2 = 10
  Profile = -> Sketch019
  ReferenceAxis = -> Sketch019 [N_Axis]
  Refine = true
  Suppressed = false
  Type = 0
FEATURE [Sketcher::SketchObject] Sketch020
  ArcFitTolerance = 1e-06
  AttachmentSupport = -> [XY_Plane007]
  ExternalGeometry = -> [Binder005]
  FullyConstrained = true
  MakeInternals = false
  MapMode = 5
  sketch-geometry (10):
    g0: LineSegment StartX=-20.965 StartY=23.285 StartZ=0 EndX=-20.965 EndY=2.51502 EndZ=0
    g1: LineSegment StartX=-13.865 StartY=-4.585 StartZ=0 EndX=14.265 EndY=-4.585 EndZ=0
    g2: LineSegment StartX=21.365 StartY=2.51502 StartZ=0 EndX=21.365 EndY=23.285 EndZ=0
    g3: LineSegment StartX=14.265 StartY=30.385 StartZ=0 EndX=-13.865 EndY=30.385 EndZ=0
    g4: ArcOfCircle CenterX=-13.865 CenterY=23.285 CenterZ=0 NormalX=0 NormalY=0 NormalZ=1 AngleXU=0 Radius=7.10002 StartAngle=1.5708 EndAngle=3.14159
    g5: ArcOfCircle CenterX=-13.865 CenterY=2.51502 CenterZ=0 NormalX=0 NormalY=0 NormalZ=1 AngleXU=0 Radius=7.10002 StartAngle=3.14159 EndAngle=4.71239
    g6: ArcOfCircle CenterX=14.265 CenterY=2.51502 CenterZ=0 NormalX=0 NormalY=0 NormalZ=1 AngleXU=0 Radius=7.10002 StartAngle=4.71239 EndAngle=6.28319
    g7: ArcOfCircle CenterX=14.265 CenterY=23.285 CenterZ=0 NormalX=0 NormalY=0 NormalZ=1 AngleXU=0 Radius=7.10002 StartAngle=0 EndAngle=1.5708
    g8: GeomPoint [constr] X=-20.965 Y=30.385 Z=0
    g9: GeomPoint [constr] X=21.365 Y=-4.585 Z=0
  constraints (24):
    c: Tangent(g0,g4) = -1.5708
    c: Tangent(g0,g5) = -1.5708
    c: Tangent(g1,g5) = -1.5708
    c: Tangent(g1,g6) = -1.5708
    c: Tangent(g2,g6) = -1.5708
    c: Tangent(g2,g7) = -1.5708
    c: Tangent(g3,g7) = -1.5708
    c: Tangent(g3,g4) = -1.5708
    c: Vertical(g0)
    c: Vertical(g2)
    c: Horizontal(g1)
    c: Horizontal(g3)
    c: Equal(g4,g5)
    c: Equal(g5,g6)
    c: Equal(g6,g7)
    c: PointOnObject(g8,g0)
    c: PointOnObject(g8,g3)
    c: PointOnObject(g9,g1)
    c: PointOnObject(g9,g2)
    c: DistanceY(g-4,g3) = 0
    c: DistanceX(g-4,g3) = 0
    c: DistanceX(g3,g-3) = 0
    c: DistanceX(g-5,g2) = 0
    c: DistanceY(g1,g-6) = 0
FEATURE [PartDesign::Pad] Pad008
  BaseFeature = -> Pad007
  Direction = (0,0,1)
  Length = 1
  Length2 = 10
  Profile = -> Sketch020
  ReferenceAxis = -> Sketch020 [N_Axis]
  Refine = true
  Reversed = true
  Suppressed = false
  Type = 0
FEATURE [PartDesign::SubShapeBinder] Binder006
  BindCopyOnChange = 0
  BindMode = 0
  ClaimChildren = false
  Context = -> Body004 [Binder006.]
  Fuse = false
  MakeFace = true
  OffsetFill = false
  OffsetIntersection = false
  OffsetJoinType = 0
  OffsetOpenResult = false
  PartialLoad = false
  Refine = true
  Relative = true
  Support = -> [Body001[Pad001.Edge12,Pad001.Edge10,Pad001.Edge7,Pad001.Edge4]]
  _Version = 2
FEATURE [Sketcher::SketchObject] Sketch021
  ArcFitTolerance = 1e-06
  AttachmentSupport = -> [XY_Plane007]
  ExternalGeometry = -> [Binder006]
  FullyConstrained = true
  MakeInternals = false
  MapMode = 5
  sketch-geometry (4):
    g0: LineSegment StartX=-1.6 StartY=24.4 StartZ=0 EndX=-1.6 EndY=1 EndZ=0
    g1: LineSegment StartX=-1.6 StartY=1 StartZ=0 EndX=18.7 EndY=1 EndZ=0
    g2: LineSegment StartX=18.7 StartY=1 StartZ=0 EndX=18.7 EndY=24.4 EndZ=0
    g3: LineSegment StartX=18.7 StartY=24.4 StartZ=0 EndX=-1.6 EndY=24.4 EndZ=0
  constraints (12):
    c: Coincident(g0,g1)
    c: Coincident(g1,g2)
    c: Coincident(g2,g3)
    c: Coincident(g3,g0)
    c: Vertical(g0)
    c: Vertical(g2)
    c: Horizontal(g1)
    c: Horizontal(g3)
    c: DistanceY(g-3,g2) = 0.2
    c: DistanceX(g-3,g2) = 0
    c: DistanceX(g0,g-3) = 0.3
    c: DistanceY(g0,g-4) = 0.2
FEATURE [PartDesign::Pocket] Pocket008
  BaseFeature = -> Pad008
  Direction = (0,0,-1)
  Length = 0.6
  Length2 = 5
  Profile = -> Sketch021
  ReferenceAxis = -> Sketch021 [N_Axis]
  Refine = true
  Suppressed = false
  Type = 0
FEATURE [PartDesign::FeatureBase] Clone
  BaseFeature = -> Body001
  Placement = pos=(-1.3,1.2,1.1) rot=(0,0,1;0rad)
  Suppressed = false
FEATURE [PartDesign::Body] Body005  label="battery_clone"
  AllowCompound = false
  Group = -> [Clone]
  Origin = -> Origin008
  Placement = pos=(-0.1,0,-0.8) rot=(0,0,1;0rad)
  Tip = -> Clone
FEATURE [Sketcher::SketchObject] Sketch022
  ArcFitTolerance = 1e-06
  AttachmentSupport = -> [XZ_Plane005]
  ExternalGeometry = -> [Pocket007]
  FullyConstrained = true
  MakeInternals = false
  MapMode = 5
  Placement = pos=(0,0,0) rot=(1,0,0;1.5708rad)
  sketch-geometry (30):
    g0: LineSegment StartX=-11.865 StartY=7.25 StartZ=0 EndX=-11.865 EndY=5.75 EndZ=0
    g1: LineSegment StartX=-10.865 StartY=4.75 StartZ=0 EndX=-6.86497 EndY=4.75 EndZ=0
    g2: LineSegment StartX=-5.86497 StartY=5.75 StartZ=0 EndX=-5.86497 EndY=7.25 EndZ=0
    g3: LineSegment StartX=-6.86497 StartY=8.25 StartZ=0 EndX=-10.865 EndY=8.25 EndZ=0
    g4: ArcOfCircle CenterX=-10.865 CenterY=7.25 CenterZ=0 NormalX=0 NormalY=0 NormalZ=1 AngleXU=0 Radius=1 StartAngle=1.5708 EndAngle=3.14159
    g5: ArcOfCircle CenterX=-10.865 CenterY=5.75 CenterZ=0 NormalX=0 NormalY=0 NormalZ=1 AngleXU=0 Radius=1 StartAngle=3.14159 EndAngle=4.71239
    g6: ArcOfCircle CenterX=-6.86497 CenterY=5.75 CenterZ=0 NormalX=0 NormalY=0 NormalZ=1 AngleXU=0 Radius=1 StartAngle=4.71239 EndAngle=6.28319
    g7: ArcOfCircle CenterX=-6.86497 CenterY=7.25 CenterZ=0 NormalX=0 NormalY=0 NormalZ=1 AngleXU=0 Radius=1 StartAngle=0 EndAngle=1.5708
    g8: GeomPoint [constr] X=-11.865 Y=8.25 Z=0
    g9: GeomPoint [constr] X=-5.86497 Y=4.75 Z=0
    g10: LineSegment StartX=-3 StartY=7.25 StartZ=0 EndX=-3 EndY=5.75 EndZ=0
    g11: LineSegment StartX=-2 StartY=4.75 StartZ=0 EndX=2 EndY=4.75 EndZ=0
    g12: LineSegment StartX=3 StartY=5.75 StartZ=0 EndX=3 EndY=7.25 EndZ=0
    g13: LineSegment StartX=2 StartY=8.25 StartZ=0 EndX=-2 EndY=8.25 EndZ=0
    g14: ArcOfCircle CenterX=-2 CenterY=7.25 CenterZ=0 NormalX=0 NormalY=0 NormalZ=1 AngleXU=0 Radius=1 StartAngle=1.5708 EndAngle=3.14159
    g15: ArcOfCircle CenterX=-2 CenterY=5.75 CenterZ=0 NormalX=0 NormalY=0 NormalZ=1 AngleXU=0 Radius=1 StartAngle=3.14159 EndAngle=4.71239
    g16: ArcOfCircle CenterX=2 CenterY=5.75 CenterZ=0 NormalX=0 NormalY=0 NormalZ=1 AngleXU=0 Radius=1 StartAngle=4.71239 EndAngle=6.28319
    g17: ArcOfCircle CenterX=2 CenterY=7.25 CenterZ=0 NormalX=0 NormalY=0 NormalZ=1 AngleXU=0 Radius=1 StartAngle=1e-16 EndAngle=1.5708
    g18: GeomPoint [constr] X=-3 Y=8.25 Z=0
    g19: GeomPoint [constr] X=3 Y=4.75 Z=0
    g20: LineSegment StartX=6.265 StartY=7.25 StartZ=0 EndX=6.265 EndY=5.75 EndZ=0
    g21: LineSegment StartX=7.265 StartY=4.75 StartZ=0 EndX=11.265 EndY=4.75 EndZ=0
    g22: LineSegment StartX=12.265 StartY=5.75 StartZ=0 EndX=12.265 EndY=7.25 EndZ=0
    g23: LineSegment StartX=11.265 StartY=8.25 StartZ=0 EndX=7.265 EndY=8.25 EndZ=0
    g24: ArcOfCircle CenterX=7.265 CenterY=7.25 CenterZ=0 NormalX=0 NormalY=0 NormalZ=1 AngleXU=0 Radius=1 StartAngle=1.5708 EndAngle=3.14159
    g25: ArcOfCircle CenterX=7.265 CenterY=5.75 CenterZ=0 NormalX=0 NormalY=0 NormalZ=1 AngleXU=0 Radius=1 StartAngle=3.14159 EndAngle=4.71239
    g26: ArcOfCircle CenterX=11.265 CenterY=5.75 CenterZ=0 NormalX=0 NormalY=0 NormalZ=1 AngleXU=0 Radius=1 StartAngle=4.71239 EndAngle=6.28319
    g27: ArcOfCircle CenterX=11.265 CenterY=7.25 CenterZ=0 NormalX=0 NormalY=0 NormalZ=1 AngleXU=0 Radius=1 StartAngle=8e-16 EndAngle=1.5708
    g28: GeomPoint [constr] X=6.265 Y=8.25 Z=0
    g29: GeomPoint [constr] X=12.265 Y=4.75 Z=0
  constraints (72):
    c: Tangent(g0,g4) = -1.5708
    c: Tangent(g0,g5) = -1.5708
    c: Tangent(g1,g5) = -1.5708
    c: Tangent(g1,g6) = -1.5708
    c: Tangent(g2,g6) = -1.5708
    c: Tangent(g2,g7) = -1.5708
    c: Tangent(g3,g7) = -1.5708
    c: Tangent(g3,g4) = -1.5708
    c: Vertical(g0)
    c: Vertical(g2)
    c: Horizontal(g1)
    c: Horizontal(g3)
    c: Equal(g4,g5)
    c: Equal(g5,g6)
    c: Equal(g6,g7)
    c: PointOnObject(g8,g0)
    c: PointOnObject(g8,g3)
    c: PointOnObject(g9,g1)
    c: PointOnObject(g9,g2)
    c: Tangent(g10,g14) = -1.5708
    c: Tangent(g10,g15) = -1.5708
    c: Tangent(g11,g15) = -1.5708
    c: Tangent(g11,g16) = -1.5708
    c: Tangent(g12,g16) = -1.5708
    c: Tangent(g12,g17) = -1.5708
    c: Tangent(g13,g17) = -1.5708
    c: Tangent(g13,g14) = -1.5708
    c: Vertical(g10)
    c: Vertical(g12)
    c: Horizontal(g11)
    c: Horizontal(g13)
    c: Equal(g14,g15)
    c: Equal(g15,g16)
    c: Equal(g16,g17)
    c: PointOnObject(g18,g10)
    c: PointOnObject(g18,g13)
    c: PointOnObject(g19,g11)
    c: PointOnObject(g19,g12)
    c: Radius(g15) = 1
    c: Tangent(g20,g24) = -1.5708
    c: Tangent(g20,g25) = -1.5708
    c: Tangent(g21,g25) = -1.5708
    c: Tangent(g21,g26) = -1.5708
    c: Tangent(g22,g26) = -1.5708
    c: Tangent(g22,g27) = -1.5708
    c: Tangent(g23,g27) = -1.5708
    c: Tangent(g23,g24) = -1.5708
    c: Vertical(g20)
    c: Vertical(g22)
    c: Horizontal(g21)
    c: Horizontal(g23)
    c: Equal(g24,g25)
    c: Equal(g25,g26)
    c: Equal(g26,g27)
    c: PointOnObject(g28,g20)
    c: PointOnObject(g28,g23)
    c: PointOnObject(g29,g21)
    c: PointOnObject(g29,g22)
    c: Radius(g25) = 1
    c: Equal(g23,g13)
    c: Equal(g13,g3)
    c: Equal(g2,g12)
    c: Equal(g12,g22)
    c: DistanceY(g11,g13) = 3.5
    c: DistanceX(g10,g12) = 6
    c: Radius(g5) = 1
    c: DistanceY(g23,g13) = 0
    c: DistanceY(g13,g3) = 0
    c: DistanceX(g-1,g12) = 3
    c: DistanceX(g22,g-5) = 2
    c: DistanceX(g-3,g0) = 2
    c: DistanceY(g-1,g21) = 4.75
FEATURE [PartDesign::Pocket] Pocket009
  BaseFeature = -> Pocket007
  Direction = (0,1,-2e-16)
  Length = 5
  Length2 = 5
  Profile = -> Sketch022
  ReferenceAxis = -> Sketch022 [N_Axis]
  Refine = true
  Reversed = true
  Suppressed = false
  Type = 0
FEATURE [PartDesign::SubShapeBinder] Binder007
  BindCopyOnChange = 0
  BindMode = 0
  ClaimChildren = false
  Context = -> Body004 [Binder007.]
  Fuse = false
  MakeFace = true
  OffsetFill = false
  OffsetIntersection = false
  OffsetJoinType = 0
  OffsetOpenResult = false
  PartialLoad = false
  Refine = true
  Relative = true
  Support = -> [Body002[Pocket009.Edge113,Pocket009.Edge109,Pocket009.Edge111,Pocket009.Edge115,Pocket009.Edge103,Pocket009.Edge105,Pocket009.Edge101,Pocket009.Edge107]]
  _Version = 2
FEATURE [Sketcher::SketchObject] Sketch023
  ArcFitTolerance = 1e-06
  AttachmentSupport = -> [XZ_Plane007]
  ExternalGeometry = -> [Pocket008,Binder007]
  FullyConstrained = true
  MakeInternals = false
  MapMode = 5
  Placement = pos=(0,0,0) rot=(1,0,0;1.5708rad)
  sketch-geometry (16):
    g0: LineSegment StartX=-13.865 StartY=0 StartZ=0 EndX=14.265 EndY=0 EndZ=0
    g1: LineSegment StartX=14.265 StartY=0 StartZ=0 EndX=14.265 EndY=8.25 EndZ=0
    g2: LineSegment StartX=-13.865 StartY=8.25 StartZ=0 EndX=-13.865 EndY=0 EndZ=0
    g3: LineSegment StartX=-11.965 StartY=8.25 StartZ=0 EndX=-11.965 EndY=4.75 EndZ=0
    g4: LineSegment StartX=-11.965 StartY=4.75 StartZ=0 EndX=-5.76497 EndY=4.75 EndZ=0
    g5: LineSegment StartX=-5.76497 StartY=4.75 StartZ=0 EndX=-5.76497 EndY=8.25 EndZ=0
    g6: LineSegment StartX=-3.1 StartY=4.75 StartZ=0 EndX=3.1 EndY=4.75 EndZ=0
    g7: LineSegment StartX=3.1 StartY=4.75 StartZ=0 EndX=3.1 EndY=8.25 EndZ=0
    g8: LineSegment StartX=-3.1 StartY=8.25 StartZ=0 EndX=-3.1 EndY=4.75 EndZ=0
    g9: LineSegment StartX=6.165 StartY=4.75 StartZ=0 EndX=12.365 EndY=4.75 EndZ=0
    g10: LineSegment StartX=12.365 StartY=4.75 StartZ=0 EndX=12.365 EndY=8.25 EndZ=0
    g11: LineSegment StartX=6.165 StartY=8.25 StartZ=0 EndX=6.165 EndY=4.75 EndZ=0
    g12: LineSegment StartX=12.365 StartY=8.25 StartZ=0 EndX=14.265 EndY=8.25 EndZ=0
    g13: LineSegment StartX=-11.965 StartY=8.25 StartZ=0 EndX=-13.865 EndY=8.25 EndZ=0
    g14: LineSegment StartX=-5.76497 StartY=8.25 StartZ=0 EndX=-3.1 EndY=8.25 EndZ=0
    g15: LineSegment StartX=6.165 StartY=8.25 StartZ=0 EndX=3.1 EndY=8.25 EndZ=0
  constraints (47):
    c: Coincident(g0,g1)
    c: Coincident(g2,g0)
    c: Horizontal(g0)
    c: Vertical(g1)
    c: Vertical(g2)
    c: Coincident(g0,g-3)
    c: DistanceX(g0,g-3) = 0
    c: Coincident(g3,g4)
    c: Coincident(g4,g5)
    c: Vertical(g3)
    c: Vertical(g5)
    c: Horizontal(g4)
    c: Coincident(g6,g7)
    c: Coincident(g8,g6)
    c: Horizontal(g6)
    c: Vertical(g7)
    c: Vertical(g8)
    c: Coincident(g9,g10)
    c: Coincident(g11,g9)
    c: Horizontal(g9)
    c: Vertical(g10)
    c: Vertical(g11)
    c: DistanceX(g3,g5) = 6.2
    c: DistanceY(g5,g5) = 3.5
    c: Equal(g5,g7)
    c: Equal(g7,g10)
    c: DistanceX(g9,g-13) = 0.1
    c: DistanceX(g6,g-10) = 0.1
    c: DistanceX(g3,g-7) = 0.1
    c: DistanceY(g7,g-5) = 0
    c: Coincident(g12,g10)
    c: Coincident(g12,g1)
    c: Parallel(g12,g-1)
    c: Coincident(g13,g3)
    c: Coincident(g13,g2)
    c: Parallel(g13,g-1)
    c: Coincident(g14,g5)
    c: Coincident(g14,g8)
    c: Coincident(g15,g11)
    c: Coincident(g15,g7)
    c: Parallel(g15,g14)
    c: Parallel(g14,g13)
    c: DistanceY(g7,g8) = 0
    c: DistanceY(g10,g3) = 0
    c: DistanceY(g9,g6) = 0
    c: DistanceX(g-12,g6) = 0.1
    c: DistanceX(g-15,g9) = 0.1
FEATURE [PartDesign::Pad] Pad009
  BaseFeature = -> Pocket008
  Direction = (0,-1,2e-16)
  Length = 3
  Length2 = 10
  Profile = -> Sketch023
  ReferenceAxis = -> Sketch023 [N_Axis]
  Refine = true
  Suppressed = false
  Type = 0
FEATURE [Sketcher::SketchObject] Sketch024
  ArcFitTolerance = 1e-06
  AttachmentSupport = -> [XZ_Plane007]
  ExternalGeometry = -> [Pad009]
  FullyConstrained = true
  MakeInternals = false
  MapMode = 5
  Placement = pos=(0,0,0) rot=(1,0,0;1.5708rad)
  sketch-geometry (12):
    g0: LineSegment StartX=-12.465 StartY=7.1 StartZ=0 EndX=-12.465 EndY=5.9 EndZ=0
    g1: LineSegment StartX=-12.465 StartY=5.9 StartZ=0 EndX=-5.26497 EndY=5.9 EndZ=0
    g2: LineSegment StartX=-5.26497 StartY=5.9 StartZ=0 EndX=-5.26497 EndY=7.1 EndZ=0
    g3: LineSegment StartX=-5.26497 StartY=7.1 StartZ=0 EndX=-12.465 EndY=7.1 EndZ=0
    g4: LineSegment StartX=-3.6 StartY=5.9 StartZ=0 EndX=3.6 EndY=5.9 EndZ=0
    g5: LineSegment StartX=3.6 StartY=5.9 StartZ=0 EndX=3.6 EndY=7.1 EndZ=0
    g6: LineSegment StartX=3.6 StartY=7.1 StartZ=0 EndX=-3.6 EndY=7.1 EndZ=0
    g7: LineSegment StartX=-3.6 StartY=7.1 StartZ=0 EndX=-3.6 EndY=5.9 EndZ=0
    g8: LineSegment StartX=5.665 StartY=7.1 StartZ=0 EndX=5.665 EndY=5.9 EndZ=0
    g9: LineSegment StartX=5.665 StartY=5.9 StartZ=0 EndX=12.865 EndY=5.9 EndZ=0
    g10: LineSegment StartX=12.865 StartY=5.9 StartZ=0 EndX=12.865 EndY=7.1 EndZ=0
    g11: LineSegment StartX=12.865 StartY=7.1 StartZ=0 EndX=5.665 EndY=7.1 EndZ=0
  constraints (36):
    c: Coincident(g0,g1)
    c: Coincident(g1,g2)
    c: Coincident(g2,g3)
    c: Coincident(g3,g0)
    c: Vertical(g0)
    c: Vertical(g2)
    c: Horizontal(g1)
    c: Horizontal(g3)
    c: Coincident(g4,g5)
    c: Coincident(g5,g6)
    c: Coincident(g6,g7)
    c: Coincident(g7,g4)
    c: Horizontal(g4)
    c: Horizontal(g6)
    c: Vertical(g5)
    c: Vertical(g7)
    c: Coincident(g8,g9)
    c: Coincident(g9,g10)
    c: Coincident(g10,g11)
    c: Coincident(g11,g8)
    c: Vertical(g8)
    c: Vertical(g10)
    c: Horizontal(g9)
    c: Horizontal(g11)
    c: DistanceY(g8,g5) = 0
    c: DistanceY(g2,g6) = 0
    c: Equal(g2,g7)
    c: Equal(g5,g8)
    c: DistanceY(g8,g8) = 1.2
    c: DistanceX(g-3,g1) = 0.5
    c: DistanceX(g0,g-4) = 0.5
    c: DistanceX(g6,g-8) = 0.5
    c: DistanceX(g-5,g5) = 0.5
    c: DistanceX(g8,g-6) = 0.5
    c: DistanceX(g-7,g10) = 0.5
    c: DistanceY(g2,g-3) = 1.15
FEATURE [PartDesign::Pocket] Pocket010
  BaseFeature = -> Pad009
  Direction = (0,1,-2e-16)
  Length = 1.2
  Length2 = 5
  Profile = -> Sketch024
  ReferenceAxis = -> Sketch024 [N_Axis]
  Refine = true
  Reversed = true
  Suppressed = false
  Type = 0
FEATURE [PartDesign::SubShapeBinder] Binder008
  BindCopyOnChange = 0
  BindMode = 0
  ClaimChildren = false
  Context = -> Body006 [Binder008.]
  Fuse = false
  MakeFace = true
  OffsetFill = false
  OffsetIntersection = false
  OffsetJoinType = 0
  OffsetOpenResult = false
  PartialLoad = false
  Refine = true
  Relative = true
  Support = -> [Body002[Pocket011.Edge68,Pocket011.Edge64,Pocket011.Edge52,Pocket011.Edge48,Pocket011.Edge51,Pocket011.Edge54,Pocket011.Edge50,Pocket011.Edge66]]
  _Version = 2
FEATURE [PartDesign::SubShapeBinder] Binder009
  BindCopyOnChange = 0
  BindMode = 0
  ClaimChildren = false
  Context = -> Body006 [Binder009.]
  Fuse = false
  MakeFace = true
  OffsetFill = false
  OffsetIntersection = false
  OffsetJoinType = 0
  OffsetOpenResult = false
  PartialLoad = false
  Refine = true
  Relative = true
  Support = -> [Body002[Pocket011.Edge105,Pocket011.Edge101,Pocket011.Edge93,Pocket011.Edge97,Pocket011.Edge99,Pocket011.Edge95,Pocket011.Edge115,Pocket011.Edge114]]
  _Version = 2
FEATURE [Sketcher::SketchObject] Sketch026
  ArcFitTolerance = 1e-06
  AttachmentSupport = -> [XZ_Plane009]
  ExternalGeometry = -> [Binder008]
  FullyConstrained = true
  MakeInternals = false
  MapMode = 5
  Placement = pos=(0,0,0) rot=(1,0,0;1.5708rad)
  sketch-geometry (10):
    g0: LineSegment StartX=6.165 StartY=8.15 StartZ=0 EndX=6.165 EndY=6.65 EndZ=0
    g1: LineSegment StartX=7.265 StartY=5.55 StartZ=0 EndX=11.265 EndY=5.55 EndZ=0
    g2: LineSegment StartX=12.365 StartY=6.65 StartZ=0 EndX=12.365 EndY=8.15 EndZ=0
    g3: LineSegment StartX=11.265 StartY=9.25 StartZ=0 EndX=7.265 EndY=9.25 EndZ=0
    g4: ArcOfCircle CenterX=7.265 CenterY=8.15 CenterZ=0 NormalX=0 NormalY=0 NormalZ=1 AngleXU=0 Radius=1.1 StartAngle=1.5708 EndAngle=3.14159
    g5: ArcOfCircle CenterX=7.265 CenterY=6.65 CenterZ=0 NormalX=0 NormalY=0 NormalZ=1 AngleXU=0 Radius=1.1 StartAngle=3.14159 EndAngle=4.71239
    g6: ArcOfCircle CenterX=11.265 CenterY=6.65 CenterZ=0 NormalX=0 NormalY=0 NormalZ=1 AngleXU=0 Radius=1.1 StartAngle=4.71239 EndAngle=6.28319
    g7: ArcOfCircle CenterX=11.265 CenterY=8.15 CenterZ=0 NormalX=0 NormalY=0 NormalZ=1 AngleXU=0 Radius=1.1 StartAngle=0 EndAngle=1.5708
    g8: GeomPoint [constr] X=6.165 Y=9.25 Z=0
    g9: GeomPoint [constr] X=12.365 Y=5.55 Z=0
  constraints (24):
    c: Tangent(g0,g4) = -1.5708
    c: Tangent(g0,g5) = -1.5708
    c: Tangent(g1,g5) = -1.5708
    c: Tangent(g1,g6) = -1.5708
    c: Tangent(g2,g6) = -1.5708
    c: Tangent(g2,g7) = -1.5708
    c: Tangent(g3,g7) = -1.5708
    c: Tangent(g3,g4) = -1.5708
    c: Vertical(g0)
    c: Vertical(g2)
    c: Horizontal(g1)
    c: Horizontal(g3)
    c: Equal(g4,g5)
    c: Equal(g5,g6)
    c: Equal(g6,g7)
    c: PointOnObject(g8,g0)
    c: PointOnObject(g8,g3)
    c: PointOnObject(g9,g1)
    c: PointOnObject(g9,g2)
    c: DistanceY(g0,g-3) = 0
    c: DistanceX(g1,g-7) = 0
    c: DistanceX(g-5,g3) = 0
    c: DistanceY(g3,g-5) = 0.4
    c: DistanceY(g-7,g1) = 0.4
FEATURE [Sketcher::SketchObject] Sketch027
  ArcFitTolerance = 1e-06
  AttachmentSupport = -> [XZ_Plane009]
  ExternalGeometry = -> [Binder009]
  FullyConstrained = true
  MakeInternals = false
  MapMode = 5
  Placement = pos=(0,0,0) rot=(1,0,0;1.5708rad)
  sketch-geometry (10):
    g0: LineSegment StartX=6.515 StartY=8.15 StartZ=0 EndX=6.515 EndY=6.65 EndZ=0
    g1: LineSegment StartX=7.265 StartY=5.9 StartZ=0 EndX=11.265 EndY=5.9 EndZ=0
    g2: LineSegment StartX=12.015 StartY=6.65 StartZ=0 EndX=12.015 EndY=8.15 EndZ=0
    g3: LineSegment StartX=11.265 StartY=8.9 StartZ=0 EndX=7.265 EndY=8.9 EndZ=0
    g4: ArcOfCircle CenterX=7.265 CenterY=8.15 CenterZ=0 NormalX=0 NormalY=0 NormalZ=1 AngleXU=0 Radius=0.75 StartAngle=1.5708 EndAngle=3.14159
    g5: ArcOfCircle CenterX=7.265 CenterY=6.65 CenterZ=0 NormalX=0 NormalY=0 NormalZ=1 AngleXU=0 Radius=0.75 StartAngle=3.14159 EndAngle=4.71239
    g6: ArcOfCircle CenterX=11.265 CenterY=6.65 CenterZ=0 NormalX=0 NormalY=0 NormalZ=1 AngleXU=0 Radius=0.75 StartAngle=4.71239 EndAngle=6.28319
    g7: ArcOfCircle CenterX=11.265 CenterY=8.15 CenterZ=0 NormalX=0 NormalY=0 NormalZ=1 AngleXU=0 Radius=0.75 StartAngle=-9e-16 EndAngle=1.5708
    g8: GeomPoint [constr] X=6.515 Y=8.9 Z=0
    g9: GeomPoint [constr] X=12.015 Y=5.9 Z=0
  constraints (24):
    c: Tangent(g0,g4) = -1.5708
    c: Tangent(g0,g5) = -1.5708
    c: Tangent(g1,g5) = -1.5708
    c: Tangent(g1,g6) = -1.5708
    c: Tangent(g2,g6) = -1.5708
    c: Tangent(g2,g7) = -1.5708
    c: Tangent(g3,g7) = -1.5708
    c: Tangent(g3,g4) = -1.5708
    c: Vertical(g0)
    c: Vertical(g2)
    c: Horizontal(g1)
    c: Horizontal(g3)
    c: Equal(g4,g5)
    c: Equal(g5,g6)
    c: Equal(g6,g7)
    c: PointOnObject(g8,g0)
    c: PointOnObject(g8,g3)
    c: PointOnObject(g9,g1)
    c: PointOnObject(g9,g2)
    c: DistanceY(g2,g-5) = 0
    c: DistanceX(g3,g-3) = 0
    c: DistanceX(g-3,g3) = 0
    c: DistanceY(g-7,g0) = 0
    c: DistanceY(g-6,g1) = 0.25
FEATURE [PartDesign::Pad] Pad010
  Direction = (0,-1,2e-16)
  Length = 3.5
  Length2 = -3.08
  Placement = pos=(0,0,0) rot=(1,0,0;1.5708rad)
  Profile = -> Sketch026
  ReferenceAxis = -> Sketch026 [N_Axis]
  Refine = true
  Suppressed = false
  Type = 4
FEATURE [PartDesign::Pad] Pad011
  BaseFeature = -> Pad010
  Direction = (0,-1,2e-16)
  Length = 6
  Length2 = -3.5
  Placement = pos=(0,0,0) rot=(1,0,0;1.5708rad)
  Profile = -> Sketch027
  ReferenceAxis = -> Sketch027 [N_Axis]
  Refine = true
  Suppressed = false
  Type = 4
FEATURE [PartDesign::Body] Body006  label="button_base"
  AllowCompound = false
  Group = -> [Binder008,Binder009,Sketch026,Sketch027,Pad010,Pad011]
  Origin = -> Origin009
  Placement = pos=(0,-0.68,0) rot=(0,0,1;0rad)
  Tip = -> Pad011
FEATURE [PartDesign::FeatureBase] Clone001
  BaseFeature = -> Body006
  Suppressed = false
FEATURE [Sketcher::SketchObject] Sketch028
  ArcFitTolerance = 1e-06
  AttachmentSupport = -> [XZ_Plane010]
  ExternalGeometry = -> [Clone001]
  FullyConstrained = false
  MakeInternals = false
  MapMode = 5
  Placement = pos=(0,0,0) rot=(1,0,0;1.5708rad)
  sketch-geometry (6):
    g0: LineSegment StartX=9.765 StartY=6.4 StartZ=0 EndX=9.765 EndY=8.4 EndZ=0
    g1: LineSegment StartX=9.765 StartY=8.4 StartZ=0 EndX=11.497 EndY=7.4 EndZ=0
    g2: LineSegment StartX=11.497 StartY=7.4 StartZ=0 EndX=9.765 EndY=6.4 EndZ=0
    g3: LineSegment StartX=7.53295 StartY=8.4 StartZ=0 EndX=7.53295 EndY=6.4 EndZ=0
    g4: LineSegment StartX=7.53295 StartY=6.4 StartZ=0 EndX=9.265 EndY=7.4 EndZ=0
    g5: LineSegment StartX=9.265 StartY=7.4 StartZ=0 EndX=7.53295 EndY=8.4 EndZ=0
  constraints (17):
    c: Vertical(g0)
    c: Coincident(g0,g1)
    c: Coincident(g1,g2)
    c: Coincident(g2,g0)
    c: Coincident(g3,g4)
    c: Coincident(g4,g5)
    c: Coincident(g5,g3)
    c: Parallel(g3,g0)
    c: Equal(g1,g0)
    c: Equal(g0,g2)
    c: Equal(g2,g3)
    c: Equal(g3,g5)
    c: Equal(g5,g4)
    c: DistanceY(g1,g4) = 0
    c: DistanceY(g0,g0) = 2
    c: DistanceX(g4,g-3) = 2
    c: DistanceX(g4,g0) = 0.5
FEATURE [PartDesign::Pocket] Pocket012
  BaseFeature = -> Clone001
  Direction = (0,1,-2e-16)
  Length = 10
  Length2 = -4.3
  Profile = -> Sketch028
  ReferenceAxis = -> Sketch028 [N_Axis]
  Refine = true
  Reversed = true
  Suppressed = false
  Type = 4
FEATURE [PartDesign::Body] Body007  label="btn_down"
  AllowCompound = false
  Group = -> [Clone001,Sketch028,Pocket012]
  Origin = -> Origin010
  Tip = -> Pocket012
FEATURE [PartDesign::FeatureBase] Clone002
  BaseFeature = -> Body007
  Suppressed = false
FEATURE [PartDesign::Body] Body008  label="btn_up"
  AllowCompound = false
  Group = -> [Clone002]
  Origin = -> Origin011
  Placement = pos=(0.4,0,14.8) rot=(0,1,0;3.14159rad)
  Tip = -> Clone002
FEATURE [PartDesign::FeatureBase] Clone003
  BaseFeature = -> Body006
  Suppressed = false
FEATURE [Sketcher::SketchObject] Sketch029
  ArcFitTolerance = 1e-06
  AttachmentSupport = -> [XZ_Plane012]
  ExternalGeometry = -> [Clone003]
  FullyConstrained = true
  MakeInternals = false
  MapMode = 5
  Placement = pos=(0,0,0) rot=(1,0,0;1.5708rad)
  sketch-geometry (21):
    g0: LineSegment StartX=8.865 StartY=6.94282 StartZ=0 EndX=8.465 EndY=7.63564 EndZ=0
    g1: LineSegment StartX=8.465 StartY=7.63564 StartZ=0 EndX=7.665 EndY=7.63564 EndZ=0
    g2: LineSegment StartX=7.665 StartY=7.63564 StartZ=0 EndX=7.265 EndY=6.94282 EndZ=0
    g3: LineSegment StartX=7.265 StartY=6.94282 StartZ=0 EndX=7.665 EndY=6.25 EndZ=0
    g4: LineSegment StartX=7.665 StartY=6.25 StartZ=0 EndX=8.465 EndY=6.25 EndZ=0
    g5: LineSegment StartX=8.465 StartY=6.25 StartZ=0 EndX=8.865 EndY=6.94282 EndZ=0
    g6: Circle [constr] CenterX=8.065 CenterY=6.94282 CenterZ=0 NormalX=0 NormalY=0 NormalZ=1 AngleXU=0 Radius=0.8
    g7: LineSegment StartX=10.015 StartY=7.85718 StartZ=0 EndX=9.615 EndY=8.55 EndZ=0
    g8: LineSegment StartX=9.615 StartY=8.55 StartZ=0 EndX=8.815 EndY=8.55 EndZ=0
    g9: LineSegment StartX=8.815 StartY=8.55 StartZ=0 EndX=8.415 EndY=7.85718 EndZ=0
    g10: LineSegment StartX=8.415 StartY=7.85718 StartZ=0 EndX=8.815 EndY=7.16436 EndZ=0
    g11: LineSegment StartX=8.815 StartY=7.16436 StartZ=0 EndX=9.615 EndY=7.16436 EndZ=0
    g12: LineSegment StartX=9.615 StartY=7.16436 StartZ=0 EndX=10.015 EndY=7.85718 EndZ=0
    g13: Circle [constr] CenterX=9.215 CenterY=7.85718 CenterZ=0 NormalX=0 NormalY=0 NormalZ=1 AngleXU=0 Radius=0.8
    g14: LineSegment StartX=11.265 StartY=6.94282 StartZ=0 EndX=10.865 EndY=7.63564 EndZ=0
    g15: LineSegment StartX=10.865 StartY=7.63564 StartZ=0 EndX=10.065 EndY=7.63564 EndZ=0
    g16: LineSegment StartX=10.065 StartY=7.63564 StartZ=0 EndX=9.665 EndY=6.94282 EndZ=0
    g17: LineSegment StartX=9.665 StartY=6.94282 StartZ=0 EndX=10.065 EndY=6.25 EndZ=0
    g18: LineSegment StartX=10.065 StartY=6.25 StartZ=0 EndX=10.865 EndY=6.25 EndZ=0
    g19: LineSegment StartX=10.865 StartY=6.25 StartZ=0 EndX=11.265 EndY=6.94282 EndZ=0
    g20: Circle [constr] CenterX=10.465 CenterY=6.94282 CenterZ=0 NormalX=0 NormalY=0 NormalZ=1 AngleXU=0 Radius=0.8
  constraints (51):
    c: Coincident(g0,g1)
    c: Coincident(g1,g2)
    c: Coincident(g2,g3)
    c: Coincident(g3,g4)
    c: Coincident(g4,g5)
    c: Coincident(g5,g0)
    c: Equal(g0, g1-g5) x5
    c: PointOnObject(g0,g6)
    c: PointOnObject(g1,g6)
    c: PointOnObject(g2,g6)
    c: PointOnObject(g3,g6)
    c: PointOnObject(g4,g6)
    c: PointOnObject(g5,g6)
    c: Radius(g6) = 0.8
    c: Coincident(g7,g8)
    c: Coincident(g8,g9)
    c: Coincident(g9,g10)
    c: Coincident(g10,g11)
    c: Coincident(g11,g12)
    c: Coincident(g12,g7)
    c: Equal(g7, g8-g12) x5
    c: PointOnObject(g7,g13)
    c: PointOnObject(g8,g13)
    c: PointOnObject(g9,g13)
    c: PointOnObject(g10,g13)
    c: PointOnObject(g11,g13)
    c: PointOnObject(g12,g13)
    c: Radius(g13) = 0.8
    c: Parallel(g1,g8)
    c: Parallel(g8,g-3)
    c: DistanceX(g-4,g2) = 0.75
    c: Coincident(g14,g15)
    c: Coincident(g15,g16)
    c: Coincident(g16,g17)
    c: Coincident(g17,g18)
    c: Coincident(g18,g19)
    c: Coincident(g19,g14)
    c: Equal(g14, g15-g19) x5
    c: PointOnObject(g14,g20)
    c: PointOnObject(g15,g20)
    c: PointOnObject(g16,g20)
    c: PointOnObject(g17,g20)
    c: PointOnObject(g18,g20)
    c: PointOnObject(g19,g20)
    c: Radius(g20) = 0.8
    c: Parallel(g15,g8)
    c: DistanceX(g14,g-6) = 0.75
    c: DistanceY(g16,g0) = 0
    c: DistanceY(g-5,g18) = 0.35
    c: DistanceY(g7,g-3) = 0.35
    c: DistanceX(g13,g20) = 1.25
FEATURE [PartDesign::Pocket] Pocket013
  BaseFeature = -> Clone003
  Direction = (0,1,-2e-16)
  Length = 10
  Length2 = -4.3
  Profile = -> Sketch029
  ReferenceAxis = -> Sketch029 [N_Axis]
  Refine = true
  Reversed = true
  Suppressed = false
  Type = 4
FEATURE [PartDesign::Body] Body009  label="btn_select"
  AllowCompound = false
  Group = -> [Clone003,Sketch029,Pocket013]
  Origin = -> Origin012
  Placement = pos=(-9.3,0,0) rot=(0,0,1;0rad)
  Tip = -> Pocket013
FEATURE [PartDesign::Fillet] Fillet002
  Base = -> Pocket010 [Edge43,Edge45,Edge49,Edge53,Edge56,Edge55,Edge51,Edge47]
  BaseFeature = -> Pocket010
  Radius = 0.9
  Refine = true
  SupportTransform = false
  Suppressed = false
  UseAllEdges = false
FEATURE [PartDesign::Body] Body004  label="backplate"
  AllowCompound = false
  Group = -> [Binder005,Sketch019,Pad007,Sketch020,Pad008,Sketch021,Binder006,Pocket008,Binder007,Sketch023,Pad009,Sketch024,Pocket010,Fillet002]
  Origin = -> Origin007
  Placement = pos=(0,0,0.9) rot=(0,0,1;0rad)
  Tip = -> Fillet002
FEATURE [Sketcher::SketchObject] Sketch030
  ArcFitTolerance = 1e-06
  AttachmentSupport = -> [XZ_Plane005]
  ExternalGeometry = -> [Pocket009]
  FullyConstrained = true
  MakeInternals = false
  MapMode = 5
  Placement = pos=(0,0,0) rot=(1,0,0;1.5708rad)
  sketch-geometry (30):
    g0: LineSegment StartX=11.265 StartY=8.75 StartZ=0 EndX=7.265 EndY=8.75 EndZ=0
    g1: LineSegment StartX=5.765 StartY=7.25 StartZ=0 EndX=5.765 EndY=5.75 EndZ=0
    g2: LineSegment StartX=7.265 StartY=4.25 StartZ=0 EndX=11.265 EndY=4.25 EndZ=0
    g3: LineSegment StartX=12.765 StartY=5.75 StartZ=0 EndX=12.765 EndY=7.25 EndZ=0
    g4: ArcOfCircle CenterX=11.265 CenterY=7.25 CenterZ=0 NormalX=0 NormalY=0 NormalZ=1 AngleXU=0 Radius=1.5 StartAngle=0 EndAngle=1.5708
    g5: ArcOfCircle CenterX=7.265 CenterY=7.25 CenterZ=0 NormalX=0 NormalY=0 NormalZ=1 AngleXU=0 Radius=1.5 StartAngle=1.5708 EndAngle=3.14159
    g6: ArcOfCircle CenterX=7.265 CenterY=5.75 CenterZ=0 NormalX=0 NormalY=0 NormalZ=1 AngleXU=0 Radius=1.5 StartAngle=3.14159 EndAngle=4.71239
    g7: ArcOfCircle CenterX=11.265 CenterY=5.75 CenterZ=0 NormalX=0 NormalY=0 NormalZ=1 AngleXU=0 Radius=1.5 StartAngle=4.71239 EndAngle=6.28319
    g8: GeomPoint [constr] X=12.765 Y=8.75 Z=0
    g9: GeomPoint [constr] X=5.765 Y=4.25 Z=0
    g10: LineSegment StartX=-12.365 StartY=7.25 StartZ=0 EndX=-12.365 EndY=5.75 EndZ=0
    g11: LineSegment StartX=-10.865 StartY=4.25 StartZ=0 EndX=-6.86497 EndY=4.25 EndZ=0
    g12: LineSegment StartX=-5.36497 StartY=5.75 StartZ=0 EndX=-5.36497 EndY=7.25 EndZ=0
    g13: LineSegment StartX=-6.86497 StartY=8.75 StartZ=0 EndX=-10.865 EndY=8.75 EndZ=0
    g14: ArcOfCircle CenterX=-10.865 CenterY=7.25 CenterZ=0 NormalX=0 NormalY=0 NormalZ=1 AngleXU=0 Radius=1.5 StartAngle=1.5708 EndAngle=3.14159
    g15: ArcOfCircle CenterX=-10.865 CenterY=5.75 CenterZ=0 NormalX=0 NormalY=0 NormalZ=1 AngleXU=0 Radius=1.5 StartAngle=3.14159 EndAngle=4.71239
    g16: ArcOfCircle CenterX=-6.86497 CenterY=5.75 CenterZ=0 NormalX=0 NormalY=0 NormalZ=1 AngleXU=0 Radius=1.5 StartAngle=4.71239 EndAngle=6.28319
    g17: ArcOfCircle CenterX=-6.86497 CenterY=7.25 CenterZ=0 NormalX=0 NormalY=0 NormalZ=1 AngleXU=0 Radius=1.5 StartAngle=-9e-16 EndAngle=1.5708
    g18: GeomPoint [constr] X=-12.365 Y=8.75 Z=0
    g19: GeomPoint [constr] X=-5.36497 Y=4.25 Z=0
    g20: LineSegment StartX=-3.5 StartY=7.25 StartZ=0 EndX=-3.5 EndY=5.75 EndZ=0
    g21: LineSegment StartX=-2 StartY=4.25 StartZ=0 EndX=2 EndY=4.25 EndZ=0
    g22: LineSegment StartX=3.5 StartY=5.75 StartZ=0 EndX=3.5 EndY=7.25 EndZ=0
    g23: LineSegment StartX=2 StartY=8.75 StartZ=0 EndX=-2 EndY=8.75 EndZ=0
    g24: ArcOfCircle CenterX=-2 CenterY=7.25 CenterZ=0 NormalX=0 NormalY=0 NormalZ=1 AngleXU=0 Radius=1.5 StartAngle=1.5708 EndAngle=3.14159
    g25: ArcOfCircle CenterX=-2 CenterY=5.75 CenterZ=0 NormalX=0 NormalY=0 NormalZ=1 AngleXU=0 Radius=1.5 StartAngle=3.14159 EndAngle=4.71239
    g26: ArcOfCircle CenterX=2 CenterY=5.75 CenterZ=0 NormalX=0 NormalY=0 NormalZ=1 AngleXU=0 Radius=1.5 StartAngle=4.71239 EndAngle=6.28319
    g27: ArcOfCircle CenterX=2 CenterY=7.25 CenterZ=0 NormalX=0 NormalY=0 NormalZ=1 AngleXU=0 Radius=1.5 StartAngle=2e-16 EndAngle=1.5708
    g28: GeomPoint [constr] X=-3.5 Y=8.75 Z=0
    g29: GeomPoint [constr] X=3.5 Y=4.25 Z=0
  constraints (72):
    c: Tangent(g0,g4) = -1.5708
    c: Tangent(g0,g5) = -1.5708
    c: Tangent(g1,g5) = -1.5708
    c: Tangent(g1,g6) = -1.5708
    c: Tangent(g2,g6) = -1.5708
    c: Tangent(g2,g7) = -1.5708
    c: Tangent(g3,g7) = -1.5708
    c: Tangent(g3,g4) = -1.5708
    c: Horizontal(g0)
    c: Horizontal(g2)
    c: Vertical(g1)
    c: Vertical(g3)
    c: Equal(g4,g5)
    c: Equal(g5,g6)
    c: Equal(g6,g7)
    c: PointOnObject(g8,g0)
    c: PointOnObject(g8,g3)
    c: PointOnObject(g9,g1)
    c: PointOnObject(g9,g2)
    c: DistanceX(g-3,g0) = 0
    c: DistanceX(g-3,g0) = 0
    c: DistanceY(g-5,g1) = 0
    c: DistanceY(g-5,g1) = 0
    c: DistanceY(g-3,g0) = 0.5
    c: Tangent(g10,g14) = -1.5708
    c: Tangent(g10,g15) = -1.5708
    c: Tangent(g11,g15) = -1.5708
    c: Tangent(g11,g16) = -1.5708
    c: Tangent(g12,g16) = -1.5708
    c: Tangent(g12,g17) = -1.5708
    c: Tangent(g13,g17) = -1.5708
    c: Tangent(g13,g14) = -1.5708
    c: Vertical(g10)
    c: Vertical(g12)
    c: Horizontal(g11)
    c: Horizontal(g13)
    c: Equal(g14,g15)
    c: Equal(g15,g16)
    c: Equal(g16,g17)
    c: PointOnObject(g18,g10)
    c: PointOnObject(g18,g13)
    c: PointOnObject(g19,g11)
    c: PointOnObject(g19,g12)
    c: Tangent(g20,g24) = -1.5708
    c: Tangent(g20,g25) = -1.5708
    c: Tangent(g21,g25) = -1.5708
    c: Tangent(g21,g26) = -1.5708
    c: Tangent(g22,g26) = -1.5708
    c: Tangent(g22,g27) = -1.5708
    c: Tangent(g23,g27) = -1.5708
    c: Tangent(g23,g24) = -1.5708
    c: Vertical(g20)
    c: Vertical(g22)
    c: Horizontal(g21)
    c: Horizontal(g23)
    c: Equal(g24,g25)
    c: Equal(g25,g26)
    c: Equal(g26,g27)
    c: PointOnObject(g28,g20)
    c: PointOnObject(g28,g23)
    c: PointOnObject(g29,g21)
    c: PointOnObject(g29,g22)
    c: DistanceY(g-14,g10) = 0
    c: DistanceY(g10,g-14) = 0
    c: DistanceX(g13,g-12) = 0
    c: DistanceX(g-12,g13) = 0
    c: DistanceX(g23,g-7) = 0
    c: DistanceX(g-7,g23) = 0
    c: DistanceY(g-9,g20) = 0
    c: DistanceY(g20,g-9) = 0
    c: DistanceY(g-7,g23) = 0.5
    c: DistanceY(g-12,g13) = 0.5
FEATURE [PartDesign::Pocket] Pocket014
  BaseFeature = -> Pocket009
  Direction = (0,1,-2e-16)
  Length = 5
  Length2 = 5
  Profile = -> Sketch030
  ReferenceAxis = -> Sketch030 [N_Axis]
  Refine = true
  Reversed = true
  Suppressed = false
  Type = 0
FEATURE [Sketcher::SketchObject] Sketch031
  ArcFitTolerance = 1e-06
  AttachmentSupport = -> [XZ_Plane005]
  ExternalGeometry = -> [Pocket014]
  FullyConstrained = true
  MakeInternals = false
  MapMode = 5
  Placement = pos=(0,0,0) rot=(1,0,0;1.5708rad)
  sketch-geometry (60):
    g0: LineSegment StartX=5.265 StartY=7.25 StartZ=0 EndX=5.265 EndY=5.75 EndZ=0
    g1: LineSegment StartX=7.265 StartY=3.75 StartZ=0 EndX=11.265 EndY=3.75 EndZ=0
    g2: LineSegment StartX=13.265 StartY=5.75 StartZ=0 EndX=13.265 EndY=7.25 EndZ=0
    g3: LineSegment StartX=11.265 StartY=9.25 StartZ=0 EndX=7.265 EndY=9.25 EndZ=0
    g4: ArcOfCircle CenterX=7.265 CenterY=7.25 CenterZ=0 NormalX=0 NormalY=0 NormalZ=1 AngleXU=0 Radius=2 StartAngle=1.5708 EndAngle=3.14159
    g5: ArcOfCircle CenterX=7.265 CenterY=5.75 CenterZ=0 NormalX=0 NormalY=0 NormalZ=1 AngleXU=0 Radius=2 StartAngle=3.14159 EndAngle=4.71239
    g6: ArcOfCircle CenterX=11.265 CenterY=5.75 CenterZ=0 NormalX=0 NormalY=0 NormalZ=1 AngleXU=0 Radius=2 StartAngle=4.71239 EndAngle=6.28319
    g7: ArcOfCircle CenterX=11.265 CenterY=7.25 CenterZ=0 NormalX=0 NormalY=0 NormalZ=1 AngleXU=0 Radius=2 StartAngle=0 EndAngle=1.5708
    g8: GeomPoint [constr] X=5.265 Y=9.25 Z=0
    g9: GeomPoint [constr] X=13.265 Y=3.75 Z=0
    g10: LineSegment StartX=6.265 StartY=7.25 StartZ=0 EndX=6.265 EndY=5.75 EndZ=0
    g11: LineSegment StartX=7.265 StartY=4.75 StartZ=0 EndX=11.265 EndY=4.75 EndZ=0
    g12: LineSegment StartX=12.265 StartY=5.75 StartZ=0 EndX=12.265 EndY=7.25 EndZ=0
    g13: LineSegment StartX=11.265 StartY=8.25 StartZ=0 EndX=7.265 EndY=8.25 EndZ=0
    g14: ArcOfCircle CenterX=7.265 CenterY=7.25 CenterZ=0 NormalX=0 NormalY=0 NormalZ=1 AngleXU=0 Radius=1 StartAngle=1.5708 EndAngle=3.14159
    g15: ArcOfCircle CenterX=7.265 CenterY=5.75 CenterZ=0 NormalX=0 NormalY=0 NormalZ=1 AngleXU=0 Radius=1 StartAngle=3.14159 EndAngle=4.71239
    g16: ArcOfCircle CenterX=11.265 CenterY=5.75 CenterZ=0 NormalX=0 NormalY=0 NormalZ=1 AngleXU=0 Radius=1 StartAngle=4.71239 EndAngle=6.28319
    g17: ArcOfCircle CenterX=11.265 CenterY=7.25 CenterZ=0 NormalX=0 NormalY=0 NormalZ=1 AngleXU=0 Radius=1 StartAngle=4e-16 EndAngle=1.5708
    g18: GeomPoint [constr] X=6.265 Y=8.25 Z=0
    g19: GeomPoint [constr] X=12.265 Y=4.75 Z=0
    g20: LineSegment StartX=-12.865 StartY=7.25 StartZ=0 EndX=-12.865 EndY=5.75 EndZ=0
    g21: LineSegment StartX=-10.865 StartY=3.75 StartZ=0 EndX=-6.86497 EndY=3.75 EndZ=0
    g22: LineSegment StartX=-4.86497 StartY=5.75 StartZ=0 EndX=-4.86497 EndY=7.25 EndZ=0
    g23: LineSegment StartX=-6.86497 StartY=9.25 StartZ=0 EndX=-10.865 EndY=9.25 EndZ=0
    g24: ArcOfCircle CenterX=-10.865 CenterY=7.25 CenterZ=0 NormalX=0 NormalY=0 NormalZ=1 AngleXU=0 Radius=2 StartAngle=1.5708 EndAngle=3.14159
    g25: ArcOfCircle CenterX=-10.865 CenterY=5.75 CenterZ=0 NormalX=0 NormalY=0 NormalZ=1 AngleXU=0 Radius=2 StartAngle=3.14159 EndAngle=4.71239
    g26: ArcOfCircle CenterX=-6.86497 CenterY=5.75 CenterZ=0 NormalX=0 NormalY=0 NormalZ=1 AngleXU=0 Radius=2 StartAngle=4.71239 EndAngle=6.28319
    g27: ArcOfCircle CenterX=-6.86497 CenterY=7.25 CenterZ=0 NormalX=0 NormalY=0 NormalZ=1 AngleXU=0 Radius=2 StartAngle=2e-16 EndAngle=1.5708
    g28: GeomPoint [constr] X=-12.865 Y=9.25 Z=0
    g29: GeomPoint [constr] X=-4.86497 Y=3.75 Z=0
    g30: LineSegment StartX=-2 StartY=3.75 StartZ=0 EndX=2 EndY=3.75 EndZ=0
    g31: LineSegment StartX=4 StartY=5.75 StartZ=0 EndX=4 EndY=7.25 EndZ=0
    g32: LineSegment StartX=2 StartY=9.25 StartZ=0 EndX=-2 EndY=9.25 EndZ=0
    g33: LineSegment StartX=-4 StartY=7.25 StartZ=0 EndX=-4 EndY=5.75 EndZ=0
    g34: ArcOfCircle CenterX=-2 CenterY=5.75 CenterZ=0 NormalX=0 NormalY=0 NormalZ=1 AngleXU=0 Radius=2 StartAngle=3.14159 EndAngle=4.71239
    g35: ArcOfCircle CenterX=2 CenterY=5.75 CenterZ=0 NormalX=0 NormalY=0 NormalZ=1 AngleXU=0 Radius=2 StartAngle=4.71239 EndAngle=6.28319
    g36: ArcOfCircle CenterX=2 CenterY=7.25 CenterZ=0 NormalX=0 NormalY=0 NormalZ=1 AngleXU=0 Radius=2 StartAngle=1e-16 EndAngle=1.5708
    g37: ArcOfCircle CenterX=-2 CenterY=7.25 CenterZ=0 NormalX=0 NormalY=0 NormalZ=1 AngleXU=0 Radius=2 StartAngle=1.5708 EndAngle=3.14159
    g38: GeomPoint [constr] X=-4 Y=3.75 Z=0
    g39: GeomPoint [constr] X=4 Y=9.25 Z=0
    g40: LineSegment StartX=-3 StartY=7.25 StartZ=0 EndX=-3 EndY=5.75 EndZ=0
    g41: LineSegment StartX=-2 StartY=4.75 StartZ=0 EndX=2 EndY=4.75 EndZ=0
    g42: LineSegment StartX=3 StartY=5.75 StartZ=0 EndX=3 EndY=7.25 EndZ=0
    g43: LineSegment StartX=2 StartY=8.25 StartZ=0 EndX=-2 EndY=8.25 EndZ=0
    g44: ArcOfCircle CenterX=-2 CenterY=7.25 CenterZ=0 NormalX=0 NormalY=0 NormalZ=1 AngleXU=0 Radius=1 StartAngle=1.5708 EndAngle=3.14159
    g45: ArcOfCircle CenterX=-2 CenterY=5.75 CenterZ=0 NormalX=0 NormalY=0 NormalZ=1 AngleXU=0 Radius=1 StartAngle=3.14159 EndAngle=4.71239
    g46: ArcOfCircle CenterX=2 CenterY=5.75 CenterZ=0 NormalX=0 NormalY=0 NormalZ=1 AngleXU=0 Radius=1 StartAngle=4.71239 EndAngle=6.28319
    g47: ArcOfCircle CenterX=2 CenterY=7.25 CenterZ=0 NormalX=0 NormalY=0 NormalZ=1 AngleXU=0 Radius=1 StartAngle=3e-16 EndAngle=1.5708
    g48: GeomPoint [constr] X=-3 Y=8.25 Z=0
    g49: GeomPoint [constr] X=3 Y=4.75 Z=0
    g50: LineSegment StartX=-11.865 StartY=7.25 StartZ=0 EndX=-11.865 EndY=5.75 EndZ=0
    g51: LineSegment StartX=-10.865 StartY=4.75 StartZ=0 EndX=-6.86497 EndY=4.75 EndZ=0
    g52: LineSegment StartX=-5.86497 StartY=5.75 StartZ=0 EndX=-5.86497 EndY=7.25 EndZ=0
    g53: LineSegment StartX=-6.86497 StartY=8.25 StartZ=0 EndX=-10.865 EndY=8.25 EndZ=0
    g54: ArcOfCircle CenterX=-10.865 CenterY=7.25 CenterZ=0 NormalX=0 NormalY=0 NormalZ=1 AngleXU=0 Radius=1 StartAngle=1.5708 EndAngle=3.14159
    g55: ArcOfCircle CenterX=-10.865 CenterY=5.75 CenterZ=0 NormalX=0 NormalY=0 NormalZ=1 AngleXU=0 Radius=1 StartAngle=3.14159 EndAngle=4.71239
    g56: ArcOfCircle CenterX=-6.86497 CenterY=5.75 CenterZ=0 NormalX=0 NormalY=0 NormalZ=1 AngleXU=0 Radius=1 StartAngle=4.71239 EndAngle=6.28319
    g57: ArcOfCircle CenterX=-6.86497 CenterY=7.25 CenterZ=0 NormalX=0 NormalY=0 NormalZ=1 AngleXU=0 Radius=1 StartAngle=6e-16 EndAngle=1.5708
    g58: GeomPoint [constr] X=-11.865 Y=8.25 Z=0
    g59: GeomPoint [constr] X=-5.86497 Y=4.75 Z=0
  constraints (144):
    c: Tangent(g0,g4) = -1.5708
    c: Tangent(g0,g5) = -1.5708
    c: Tangent(g1,g5) = -1.5708
    c: Tangent(g1,g6) = -1.5708
    c: Tangent(g2,g6) = -1.5708
    c: Tangent(g2,g7) = -1.5708
    c: Tangent(g3,g7) = -1.5708
    c: Tangent(g3,g4) = -1.5708
    c: Vertical(g0)
    c: Vertical(g2)
    c: Horizontal(g1)
    c: Horizontal(g3)
    c: Equal(g4,g5)
    c: Equal(g5,g6)
    c: Equal(g6,g7)
    c: PointOnObject(g8,g0)
    c: PointOnObject(g8,g3)
    c: PointOnObject(g9,g1)
    c: PointOnObject(g9,g2)
    c: Tangent(g10,g14) = -1.5708
    c: Tangent(g10,g15) = -1.5708
    c: Tangent(g11,g15) = -1.5708
    c: Tangent(g11,g16) = -1.5708
    c: Tangent(g12,g16) = -1.5708
    c: Tangent(g12,g17) = -1.5708
    c: Tangent(g13,g17) = -1.5708
    c: Tangent(g13,g14) = -1.5708
    c: Vertical(g10)
    c: Vertical(g12)
    c: Horizontal(g11)
    c: Horizontal(g13)
    c: Equal(g14,g15)
    c: Equal(g15,g16)
    c: Equal(g16,g17)
    c: PointOnObject(g18,g10)
    c: PointOnObject(g18,g13)
    c: PointOnObject(g19,g11)
    c: PointOnObject(g19,g12)
    c: Tangent(g20,g24) = -1.5708
    c: Tangent(g20,g25) = -1.5708
    c: Tangent(g21,g25) = -1.5708
    c: Tangent(g21,g26) = -1.5708
    c: Tangent(g22,g26) = -1.5708
    c: Tangent(g22,g27) = -1.5708
    c: Tangent(g23,g27) = -1.5708
    c: Tangent(g23,g24) = -1.5708
    c: Vertical(g20)
    c: Vertical(g22)
    c: Horizontal(g21)
    c: Horizontal(g23)
    c: Equal(g24,g25)
    c: Equal(g25,g26)
    c: Equal(g26,g27)
    c: PointOnObject(g28,g20)
    c: PointOnObject(g28,g23)
    c: PointOnObject(g29,g21)
    c: PointOnObject(g29,g22)
    c: Tangent(g30,g34) = -1.5708
    c: Tangent(g30,g35) = -1.5708
    c: Tangent(g31,g35) = -1.5708
    c: Tangent(g31,g36) = -1.5708
    c: Tangent(g32,g36) = -1.5708
    c: Tangent(g32,g37) = -1.5708
    c: Tangent(g33,g37) = -1.5708
    c: Tangent(g33,g34) = -1.5708
    c: Horizontal(g30)
    c: Horizontal(g32)
    c: Vertical(g31)
    c: Vertical(g33)
    c: Equal(g34,g35)
    c: Equal(g35,g36)
    c: Equal(g36,g37)
    c: PointOnObject(g38,g30)
    c: PointOnObject(g38,g33)
    c: PointOnObject(g39,g31)
    c: PointOnObject(g39,g32)
    c: Tangent(g40,g44) = -1.5708
    c: Tangent(g40,g45) = -1.5708
    c: Tangent(g41,g45) = -1.5708
    c: Tangent(g41,g46) = -1.5708
    c: Tangent(g42,g46) = -1.5708
    c: Tangent(g42,g47) = -1.5708
    c: Tangent(g43,g47) = -1.5708
    c: Tangent(g43,g44) = -1.5708
    c: Vertical(g40)
    c: Vertical(g42)
    c: Horizontal(g41)
    c: Horizontal(g43)
    c: Equal(g44,g45)
    c: Equal(g45,g46)
    c: Equal(g46,g47)
    c: PointOnObject(g48,g40)
    c: PointOnObject(g48,g43)
    c: PointOnObject(g49,g41)
    c: PointOnObject(g49,g42)
    c: Tangent(g50,g54) = -1.5708
    c: Tangent(g50,g55) = -1.5708
    c: Tangent(g51,g55) = -1.5708
    c: Tangent(g51,g56) = -1.5708
    c: Tangent(g52,g56) = -1.5708
    c: Tangent(g52,g57) = -1.5708
    c: Tangent(g53,g57) = -1.5708
    c: Tangent(g53,g54) = -1.5708
    c: Vertical(g50)
    c: Vertical(g52)
    c: Horizontal(g51)
    c: Horizontal(g53)
    c: Equal(g54,g55)
    c: Equal(g55,g56)
    c: Equal(g56,g57)
    c: PointOnObject(g58,g50)
    c: PointOnObject(g58,g53)
    c: PointOnObject(g59,g51)
    c: PointOnObject(g59,g52)
    c: DistanceX(g3,g-3) = 0
    c: DistanceX(g-3,g3) = 0
    c: DistanceY(g-4,g0) = 0
    c: DistanceY(g0,g-4) = 0
    c: DistanceX(g-5,g32) = 0
    c: DistanceX(g32,g-5) = 0
    c: DistanceY(g-8,g33) = 0
    c: DistanceY(g33,g-8) = 0
    c: DistanceY(g-12,g22) = 0
    c: DistanceY(g22,g-12) = 0
    c: DistanceX(g21,g-11) = 0
    c: DistanceX(g21,g-11) = 0
    c: DistanceY(g-5,g32) = 0.5
    c: DistanceY(g-3,g3) = 0.5
    c: DistanceY(g-9,g23) = 0.5
    c: DistanceY(g10,g-4) = 0
    c: DistanceY(g-4,g10) = 0
    c: DistanceX(g3,g13) = 0
    c: DistanceX(g13,g3) = 0
    c: DistanceY(g13,g3) = 1
    c: DistanceX(g43,g32) = 0
    c: DistanceX(g32,g43) = 0
    c: DistanceY(g40,g33) = 0
    c: DistanceY(g-8,g40) = 0
    c: DistanceY(g43,g32) = 1
    c: DistanceX(g23,g53) = 0
    c: DistanceX(g53,g-9) = 0
    c: DistanceY(g-12,g52) = 0
    c: DistanceY(g-12,g52) = 0
    c: DistanceY(g53,g23) = 1
FEATURE [PartDesign::Pad] Pad012
  BaseFeature = -> Pocket014
  Direction = (0,-1,2e-16)
  Length = 5.5
  Length2 = -4.58
  Profile = -> Sketch031
  ReferenceAxis = -> Sketch031 [N_Axis]
  Refine = true
  Suppressed = false
  Type = 4
FEATURE [PartDesign::Body] Body002  label="case"
  AllowCompound = false
  Group = -> [Binder,Sketch012,Pad002,Thickness001,Binder001,Sketch013,Pocket006,Binder004,Sketch018,Pocket007,Sketch022,Pocket009,Sketch030,Pocket014,Sketch031,Pad012]
  Origin = -> Origin005
  Placement = pos=(0,0,0.9) rot=(0,0,1;0rad)
  Tip = -> Pad012
FEATURE [PartDesign::SubShapeBinder] Binder010
  BindCopyOnChange = 0
  BindMode = 0
  ClaimChildren = false
  Context = -> Body010 [Binder010.]
  Fuse = false
  MakeFace = true
  OffsetFill = false
  OffsetIntersection = false
  OffsetJoinType = 0
  OffsetOpenResult = false
  PartialLoad = false
  Refine = true
  Relative = true
  Support = -> [Body002[Pad012.Edge118,Pad012.Edge73,Pad012.Edge86,Pad012.Edge90]]
  _Version = 2
FEATURE [Sketcher::SketchObject] Sketch032
  ArcFitTolerance = 1e-06
  AttachmentSupport = -> [XY_Plane013]
  ExternalGeometry = -> [Binder010]
  FullyConstrained = false
  MakeInternals = false
  MapMode = 5
  sketch-geometry (21):
    g0: LineSegment StartX=6.265 StartY=90.085 StartZ=0 EndX=10.265 EndY=90.085 EndZ=0
    g1: LineSegment StartX=10.265 StartY=90.085 StartZ=0 EndX=10.265 EndY=80.085 EndZ=0
    g2: LineSegment StartX=11.265 StartY=80.085 StartZ=0 EndX=23.365 EndY=80.085 EndZ=0
    g3: LineSegment StartX=23.365 StartY=80.085 StartZ=0 EndX=23.365 EndY=76.085 EndZ=0
    g4: LineSegment StartX=23.365 StartY=76.085 StartZ=0 EndX=16.365 EndY=76.085 EndZ=0
    g5: LineSegment StartX=16.365 StartY=76.085 StartZ=0 EndX=16.365 EndY=65.115 EndZ=0
    g6: LineSegment StartX=16.365 StartY=65.115 StartZ=0 EndX=23.365 EndY=65.115 EndZ=0
    g7: LineSegment StartX=23.365 StartY=65.115 StartZ=0 EndX=23.365 EndY=61.115 EndZ=0
    g8: LineSegment StartX=23.365 StartY=61.115 StartZ=0 EndX=-22.965 EndY=61.115 EndZ=0
    g9: LineSegment StartX=-22.965 StartY=61.115 StartZ=0 EndX=-22.965 EndY=65.115 EndZ=0
    g10: LineSegment StartX=-22.965 StartY=65.115 StartZ=0 EndX=-16.965 EndY=65.115 EndZ=0
    g11: LineSegment StartX=-16.965 StartY=65.115 StartZ=0 EndX=-16.965 EndY=76.085 EndZ=0
    g12: LineSegment StartX=-16.965 StartY=76.085 StartZ=0 EndX=-22.965 EndY=76.085 EndZ=0
    g13: LineSegment StartX=-22.965 StartY=76.085 StartZ=0 EndX=-22.965 EndY=80.085 EndZ=0
    g14: LineSegment StartX=-12.965 StartY=76.085 StartZ=0 EndX=-12.965 EndY=65.115 EndZ=0
    g15: LineSegment StartX=-12.965 StartY=65.115 StartZ=0 EndX=12.365 EndY=65.115 EndZ=0
    g16: LineSegment StartX=12.365 StartY=65.115 StartZ=0 EndX=12.365 EndY=76.085 EndZ=0
    g17: LineSegment StartX=12.365 StartY=76.085 StartZ=0 EndX=-12.965 EndY=76.085 EndZ=0
    g18: LineSegment StartX=-22.965 StartY=80.085 StartZ=0 EndX=6.265 EndY=80.085 EndZ=0
    g19: LineSegment StartX=6.265 StartY=90.085 StartZ=0 EndX=6.265 EndY=80.085 EndZ=0
    g20: LineSegment StartX=10.265 StartY=80.085 StartZ=0 EndX=11.265 EndY=80.085 EndZ=0
  constraints (62):
    c: Horizontal(g0)
    c: Coincident(g0,g1)
    c: Vertical(g1)
    c: Horizontal(g2)
    c: Coincident(g2,g3)
    c: Vertical(g3)
    c: Coincident(g3,g4)
    c: Horizontal(g4)
    c: Coincident(g4,g5)
    c: Vertical(g5)
    c: Coincident(g5,g6)
    c: Horizontal(g6)
    c: Coincident(g6,g7)
    c: Vertical(g7)
    c: Coincident(g7,g8)
    c: Horizontal(g8)
    c: Vertical(g9)
    c: Coincident(g9,g10)
    c: Horizontal(g10)
    c: Coincident(g10,g11)
    c: Vertical(g11)
    c: Coincident(g11,g12)
    c: Horizontal(g12)
    c: Coincident(g12,g13)
    c: Vertical(g13)
    c: Coincident(g14,g15)
    c: Coincident(g15,g16)
    c: Coincident(g16,g17)
    c: Coincident(g17,g14)
    c: Vertical(g14)
    c: Vertical(g16)
    c: Horizontal(g15)
    c: Horizontal(g17)
    c: DistanceY(g2,g-4) = 8
    c: DistanceY(g16,g2) = 4
    c: Horizontal(g18)
    c: Coincident(g19,g0)
    c: Coincident(g19,g18)
    c: Parallel(g19,g-2)
    c: DistanceY(g1,g18) = 0
    c: DistanceY(g-4,g0) = 2
    c: DistanceY(g3,g3) = 4
    c: DistanceY(g7,g7) = 4
    c: Coincident(g13,g18)
    c: DistanceY(g13,g13) = 4
    c: DistanceX(g0,g0) = 4
    c: DistanceY(g-6,g7) = 8
    c: Coincident(g8,g9)
    c: DistanceX(g13,g-3) = 2
    c: DistanceX(g9,g12) = 0
    c: DistanceY(g8,g9) = 4
    c: Coincident(g20,g1)
    c: Horizontal(g20)
    c: Coincident(g2,g20)
    c: DistanceX(g0,g-4) = 4
    c: DistanceX(g-5,g2) = 2
    c: DistanceX(g3,g6) = 0
    c: DistanceX(g11,g14) = 4
    c: DistanceX(g16,g4) = 4
    c: DistanceY(g10,g14) = 0
    c: DistanceX(g10,g10) = 6
    c: DistanceX(g6,g6) = 7
FEATURE [PartDesign::Pad] Pad013
  Direction = (0,0,1)
  Length = 1.9
  Length2 = -0.1
  Profile = -> Sketch032
  ReferenceAxis = -> Sketch032 [N_Axis]
  Refine = true
  Reversed = true
  Suppressed = false
  Type = 4
FEATURE [Sketcher::SketchObject] Sketch033
  ArcFitTolerance = 1e-06
  AttachmentSupport = -> [XY_Plane013]
  ExternalGeometry = -> [Pad013,Binder010]
  FullyConstrained = true
  MakeInternals = false
  MapMode = 5
  sketch-geometry (20):
    g0: LineSegment StartX=23.365 StartY=80.085 StartZ=0 EndX=21.465 EndY=80.085 EndZ=0
    g1: LineSegment StartX=21.465 StartY=80.085 StartZ=0 EndX=21.465 EndY=76.085 EndZ=0
    g2: LineSegment StartX=21.465 StartY=76.085 StartZ=0 EndX=23.365 EndY=76.085 EndZ=0
    g3: LineSegment StartX=23.365 StartY=76.085 StartZ=0 EndX=23.365 EndY=80.085 EndZ=0
    g4: LineSegment StartX=23.365 StartY=65.115 StartZ=0 EndX=21.465 EndY=65.115 EndZ=0
    g5: LineSegment StartX=21.465 StartY=65.115 StartZ=0 EndX=21.465 EndY=61.115 EndZ=0
    g6: LineSegment StartX=21.465 StartY=61.115 StartZ=0 EndX=23.365 EndY=61.115 EndZ=0
    g7: LineSegment StartX=23.365 StartY=61.115 StartZ=0 EndX=23.365 EndY=65.115 EndZ=0
    g8: LineSegment StartX=-22.965 StartY=80.085 StartZ=0 EndX=-22.965 EndY=76.085 EndZ=0
    g9: LineSegment StartX=-22.965 StartY=76.085 StartZ=0 EndX=-21.065 EndY=76.085 EndZ=0
    g10: LineSegment StartX=-21.065 StartY=76.085 StartZ=0 EndX=-21.065 EndY=80.085 EndZ=0
    g11: LineSegment StartX=-21.065 StartY=80.085 StartZ=0 EndX=-22.965 EndY=80.085 EndZ=0
    g12: LineSegment StartX=-22.965 StartY=65.115 StartZ=0 EndX=-22.965 EndY=61.115 EndZ=0
    g13: LineSegment StartX=-22.965 StartY=61.115 StartZ=0 EndX=-21.065 EndY=61.115 EndZ=0
    g14: LineSegment StartX=-21.065 StartY=61.115 StartZ=0 EndX=-21.065 EndY=65.115 EndZ=0
    g15: LineSegment StartX=-21.065 StartY=65.115 StartZ=0 EndX=-22.965 EndY=65.115 EndZ=0
    g16: LineSegment StartX=6.265 StartY=90.085 StartZ=0 EndX=6.265 EndY=88.185 EndZ=0
    g17: LineSegment StartX=6.265 StartY=88.185 StartZ=0 EndX=10.265 EndY=88.185 EndZ=0
    g18: LineSegment StartX=10.265 StartY=88.185 StartZ=0 EndX=10.265 EndY=90.085 EndZ=0
    g19: LineSegment StartX=10.265 StartY=90.085 StartZ=0 EndX=6.265 EndY=90.085 EndZ=0
  constraints (55):
    c: Coincident(g0,g1)
    c: Coincident(g1,g2)
    c: Coincident(g2,g3)
    c: Coincident(g3,g0)
    c: Horizontal(g0)
    c: Horizontal(g2)
    c: Vertical(g1)
    c: Vertical(g3)
    c: DistanceY(g2,g-12) = 0
    c: Coincident(g4,g5)
    c: Coincident(g5,g6)
    c: Coincident(g6,g7)
    c: Coincident(g7,g4)
    c: Horizontal(g4)
    c: Horizontal(g6)
    c: Vertical(g5)
    c: Vertical(g7)
    c: Coincident(g4,g-11)
    c: PointOnObject(g5,g-9)
    c: Coincident(g8,g9)
    c: Coincident(g9,g10)
    c: Coincident(g10,g11)
    c: Coincident(g11,g8)
    c: Vertical(g8)
    c: Vertical(g10)
    c: Horizontal(g9)
    c: Horizontal(g11)
    c: Coincident(g8,g-7)
    c: PointOnObject(g9,g-6)
    c: Coincident(g12,g13)
    c: Coincident(g13,g14)
    c: Coincident(g14,g15)
    c: Coincident(g15,g12)
    c: Vertical(g12)
    c: Vertical(g14)
    c: Horizontal(g13)
    c: Horizontal(g15)
    c: Coincident(g12,g-8)
    c: PointOnObject(g13,g-9)
    c: Coincident(g16,g17)
    c: Coincident(g17,g18)
    c: Coincident(g18,g19)
    c: Coincident(g19,g16)
    c: Vertical(g16)
    c: Vertical(g18)
    c: Horizontal(g17)
    c: Horizontal(g19)
    c: Coincident(g16,g-4)
    c: PointOnObject(g17,g-5)
    c: DistanceY(g18,g18) = 1.9
    c: DistanceX(g9,g9) = 1.9
    c: DistanceX(g15,g15) = 1.9
    c: DistanceX(g0,g0) = 1.9
    c: DistanceX(g6,g6) = 1.9
    c: Coincident(g0,g-10)
FEATURE [PartDesign::Pad] Pad014
  BaseFeature = -> Pad013
  Direction = (0,0,1)
  Length = 14.5
  Length2 = 1
  Profile = -> Sketch033
  ReferenceAxis = -> Sketch033 [N_Axis]
  Refine = true
  Suppressed = false
  Type = 4
FEATURE [Sketcher::SketchObject] Sketch034
  ArcFitTolerance = 1e-06
  AttachmentSupport = -> [XY_Plane013]
  ExternalGeometry = -> [Pad014]
  FullyConstrained = true
  MakeInternals = false
  MapMode = 5
  sketch-geometry (20):
    g0: LineSegment StartX=-22.965 StartY=65.115 StartZ=0 EndX=-22.965 EndY=61.115 EndZ=0
    g1: LineSegment StartX=-22.965 StartY=61.115 StartZ=0 EndX=-18.415 EndY=61.115 EndZ=0
    g2: LineSegment StartX=-18.415 StartY=61.115 StartZ=0 EndX=-18.415 EndY=65.115 EndZ=0
    g3: LineSegment StartX=-18.415 StartY=65.115 StartZ=0 EndX=-22.965 EndY=65.115 EndZ=0
    g4: LineSegment StartX=23.365 StartY=61.115 StartZ=0 EndX=23.365 EndY=65.115 EndZ=0
    g5: LineSegment StartX=23.365 StartY=65.115 StartZ=0 EndX=16.565 EndY=65.115 EndZ=0
    g6: LineSegment StartX=16.565 StartY=65.115 StartZ=0 EndX=16.565 EndY=61.115 EndZ=0
    g7: LineSegment StartX=16.565 StartY=61.115 StartZ=0 EndX=23.365 EndY=61.115 EndZ=0
    g8: LineSegment StartX=23.365 StartY=80.085 StartZ=0 EndX=16.565 EndY=80.085 EndZ=0
    g9: LineSegment StartX=16.565 StartY=80.085 StartZ=0 EndX=16.565 EndY=76.085 EndZ=0
    g10: LineSegment StartX=16.565 StartY=76.085 StartZ=0 EndX=23.365 EndY=76.085 EndZ=0
    g11: LineSegment StartX=23.365 StartY=76.085 StartZ=0 EndX=23.365 EndY=80.085 EndZ=0
    g12: LineSegment StartX=6.265 StartY=90.085 StartZ=0 EndX=6.265 EndY=85.535 EndZ=0
    g13: LineSegment StartX=6.265 StartY=85.535 StartZ=0 EndX=10.265 EndY=85.535 EndZ=0
    g14: LineSegment StartX=10.265 StartY=85.535 StartZ=0 EndX=10.265 EndY=90.085 EndZ=0
    g15: LineSegment StartX=10.265 StartY=90.085 StartZ=0 EndX=6.265 EndY=90.085 EndZ=0
    g16: LineSegment StartX=-22.965 StartY=80.085 StartZ=0 EndX=-22.965 EndY=76.085 EndZ=0
    g17: LineSegment StartX=-22.965 StartY=76.085 StartZ=0 EndX=-18.415 EndY=76.085 EndZ=0
    g18: LineSegment StartX=-18.415 StartY=76.085 StartZ=0 EndX=-18.415 EndY=80.085 EndZ=0
    g19: LineSegment StartX=-18.415 StartY=80.085 StartZ=0 EndX=-22.965 EndY=80.085 EndZ=0
  constraints (55):
    c: Coincident(g0,g1)
    c: Coincident(g1,g2)
    c: Coincident(g2,g3)
    c: Coincident(g3,g0)
    c: Vertical(g0)
    c: Vertical(g2)
    c: Horizontal(g1)
    c: Horizontal(g3)
    c: Coincident(g0,g-16)
    c: Coincident(g4,g5)
    c: Coincident(g5,g6)
    c: Coincident(g6,g7)
    c: Coincident(g7,g4)
    c: Vertical(g4)
    c: Vertical(g6)
    c: Horizontal(g5)
    c: Horizontal(g7)
    c: Coincident(g4,g-13)
    c: Coincident(g8,g9)
    c: Coincident(g9,g10)
    c: Coincident(g10,g11)
    c: Coincident(g11,g8)
    c: Horizontal(g8)
    c: Horizontal(g10)
    c: Vertical(g9)
    c: Vertical(g11)
    c: Coincident(g8,g-10)
    c: Coincident(g12,g13)
    c: Coincident(g13,g14)
    c: Coincident(g14,g15)
    c: Coincident(g15,g12)
    c: Vertical(g12)
    c: Vertical(g14)
    c: Horizontal(g13)
    c: Horizontal(g15)
    c: Coincident(g12,g-7)
    c: Coincident(g16,g17)
    c: Coincident(g17,g18)
    c: Coincident(g18,g19)
    c: Coincident(g19,g16)
    c: Vertical(g16)
    c: Vertical(g18)
    c: Horizontal(g17)
    c: Horizontal(g19)
    c: Coincident(g16,g-4)
    c: DistanceY(g-5,g16) = 0
    c: DistanceY(g-17,g0) = 0
    c: DistanceY(g4,g-14) = 0
    c: DistanceY(g-11,g10) = 0
    c: DistanceX(g-8,g14) = 0
    c: DistanceX(g5,g5) = 6.8
    c: Equal(g10,g5)
    c: DistanceX(g19,g19) = 4.55
    c: Equal(g19,g3)
    c: DistanceY(g12,g12) = 4.55
FEATURE [PartDesign::Pad] Pad015
  BaseFeature = -> Pad014
  Direction = (0,0,1)
  Length = 14.9
  Length2 = -13.5
  Profile = -> Sketch034
  ReferenceAxis = -> Sketch034 [N_Axis]
  Refine = true
  Suppressed = false
  Type = 4
FEATURE [PartDesign::Body] Body010  label="cage"
  AllowCompound = false
  Group = -> [Binder010,Sketch032,Pad013,Sketch033,Pad014,Sketch034,Pad015]
  Origin = -> Origin013
  Placement = pos=(0,-57.7,0) rot=(0,0,1;0rad)
  Tip = -> Pad015
FEATURE [PartDesign::SubShapeBinder] Binder011
  BindCopyOnChange = 0
  BindMode = 0
  ClaimChildren = false
  Context = -> Body [Binder011.]
  Fuse = false
  MakeFace = true
  OffsetFill = false
  OffsetIntersection = false
  OffsetJoinType = 0
  OffsetOpenResult = false
  PartialLoad = false
  Refine = true
  Relative = true
  Support = -> [Body003[Pad006.Edge33,Pad006.Edge17]]
  _Version = 2
FEATURE [Sketcher::SketchObject] Sketch035
  ArcFitTolerance = 1e-06
  AttachmentSupport = -> [XY_Plane]
  ExternalGeometry = -> [Binder011]
  FullyConstrained = true
  MakeInternals = false
  MapMode = 5
  sketch-geometry (8):
    g0: LineSegment StartX=-12.5766 StartY=2.2314 StartZ=0 EndX=4.5683 EndY=2.2314 EndZ=0
    g1: LineSegment StartX=4.5683 StartY=2.2314 StartZ=0 EndX=4.5683 EndY=2.4314 EndZ=0
    g2: LineSegment StartX=4.5683 StartY=2.4314 StartZ=0 EndX=-12.5766 EndY=2.4314 EndZ=0
    g3: LineSegment StartX=-12.5766 StartY=2.4314 StartZ=0 EndX=-12.5766 EndY=2.2314 EndZ=0
    g4: LineSegment StartX=7.47334 StartY=-14.6436 StartZ=0 EndX=7.67334 EndY=-14.6436 EndZ=0
    g5: LineSegment StartX=7.67334 StartY=-14.6436 StartZ=0 EndX=7.67334 EndY=-0.673644 EndZ=0
    g6: LineSegment StartX=7.67334 StartY=-0.673644 StartZ=0 EndX=7.47334 EndY=-0.673644 EndZ=0
    g7: LineSegment StartX=7.47334 StartY=-0.673644 StartZ=0 EndX=7.47334 EndY=-14.6436 EndZ=0
  constraints (22):
    c: Coincident(g0,g1)
    c: Coincident(g1,g2)
    c: Coincident(g2,g3)
    c: Coincident(g3,g0)
    c: Horizontal(g0)
    c: Horizontal(g2)
    c: Vertical(g1)
    c: Vertical(g3)
    c: Coincident(g0,g-4)
    c: Coincident(g4,g5)
    c: Coincident(g5,g6)
    c: Coincident(g6,g7)
    c: Coincident(g7,g4)
    c: Horizontal(g4)
    c: Horizontal(g6)
    c: Vertical(g5)
    c: Vertical(g7)
    c: Coincident(g4,g-3)
    c: DistanceX(g0,g-4) = 0
    c: DistanceX(g6,g6) = 0.2
    c: DistanceY(g6,g-3) = 0
    c: DistanceY(g1,g1) = 0.2
FEATURE [PartDesign::Pocket] Pocket015
  BaseFeature = -> Pocket005
  Direction = (0,0,-1)
  Length = 5
  Length2 = 5
  Profile = -> Sketch035
  ReferenceAxis = -> Sketch035 [N_Axis]
  Refine = true
  Suppressed = false
  Type = 0
FEATURE [PartDesign::Body] Body  label="displaycase"
  AllowCompound = false
  Group = -> [Sketch,Pad,Sketch001,Thickness,Pocket,Sketch002,Pocket001,Sketch011,Pocket005,Binder011,Sketch035,Pocket015]
  Origin = -> Origin
  Placement = pos=(0.2,12.9,10) rot=(0,0,1;4.71239rad)
  Tip = -> Pocket015
FEATURE [Sketcher::SketchObject] Sketch036
  ArcFitTolerance = 1e-06
  AttachmentSupport = -> [XY_Plane006]
  ExternalGeometry = -> [Chamfer]
  FullyConstrained = true
  MakeInternals = false
  MapMode = 5
  sketch-geometry (4):
    g0: LineSegment StartX=-14.4436 StartY=6.27655 StartZ=0 EndX=-14.4436 EndY=5.42666 EndZ=0
    g1: LineSegment StartX=-14.4436 StartY=5.42666 StartZ=0 EndX=-0.473644 EndY=5.42666 EndZ=0
    g2: LineSegment StartX=-0.473644 StartY=5.42666 StartZ=0 EndX=-0.473644 EndY=6.27655 EndZ=0
    g3: LineSegment StartX=-0.473644 StartY=6.27655 StartZ=0 EndX=-14.4436 EndY=6.27655 EndZ=0
  constraints (10):
    c: Coincident(g0,g1)
    c: Coincident(g1,g2)
    c: Coincident(g2,g3)
    c: Coincident(g3,g0)
    c: Vertical(g0)
    c: Vertical(g2)
    c: Horizontal(g1)
    c: Horizontal(g3)
    c: Coincident(g0,g-6)
    c: Coincident(g1,g-3)
FEATURE [PartDesign::Pad] Pad016
  BaseFeature = -> Chamfer
  Direction = (0,0,1)
  Length = 9
  Length2 = -5.8
  Profile = -> Sketch036
  ReferenceAxis = -> Sketch036 [N_Axis]
  Refine = true
  Suppressed = false
  Type = 4
FEATURE [PartDesign::Body] Body003  label="xiao-mount"
  AllowCompound = false
  Group = -> [Binder002,Sketch014,Sketch015,Pad003,Pad004,Sketch016,Pad005,Binder003,Sketch017,Pad006,Chamfer,Sketch036,Pad016]
  Origin = -> Origin006
  Placement = pos=(0,0,-0.2) rot=(0,0,1;0rad)
  Tip = -> Pad016
FEATURE [Mesh::Feature] watch_band_clasp  label="watch-band-clasp"
FEATURE [Part::Feature] watch_band_clasp001
  shape: bbox 18.13 x 23.41 x 7 mm, 4570 faces, 0 solids (baked)
FEATURE [Sketcher::SketchObject] Sketch037
  ArcFitTolerance = 1e-06
  AttachmentSupport = -> [XY_Plane014]
  FullyConstrained = true
  MakeInternals = false
  MapMode = 5
  sketch-geometry (28):
    g0: LineSegment StartX=101.674 StartY=-89.09 StartZ=0 EndX=101.674 EndY=-87.4 EndZ=0
    g1: LineSegment StartX=101.674 StartY=-87.4 StartZ=0 EndX=119.794 EndY=-87.4 EndZ=0
    g2: LineSegment StartX=119.794 StartY=-87.4 StartZ=0 EndX=119.794 EndY=-89.09 EndZ=0
    g3: LineSegment StartX=119.794 StartY=-89.09 StartZ=0 EndX=114.004 EndY=-89.09 EndZ=0
    g4: LineSegment StartX=114.004 StartY=-89.09 StartZ=0 EndX=114.004 EndY=-93.41 EndZ=0
    g5: LineSegment StartX=114.004 StartY=-93.41 StartZ=0 EndX=119.794 EndY=-93.41 EndZ=0
    g6: LineSegment StartX=119.794 StartY=-93.41 StartZ=0 EndX=119.794 EndY=-95.15 EndZ=0
    g7: LineSegment StartX=119.794 StartY=-95.15 StartZ=0 EndX=113.474 EndY=-95.15 EndZ=0
    g8: LineSegment StartX=113.474 StartY=-95.15 StartZ=0 EndX=113.474 EndY=-103.22 EndZ=0
    g9: LineSegment StartX=113.474 StartY=-103.22 StartZ=0 EndX=119.794 EndY=-103.22 EndZ=0
    g10: LineSegment StartX=119.794 StartY=-103.22 StartZ=0 EndX=119.794 EndY=-105.08 EndZ=0
    g11: LineSegment StartX=119.794 StartY=-105.08 StartZ=0 EndX=114.004 EndY=-105.08 EndZ=0
    g12: LineSegment StartX=114.004 StartY=-105.08 StartZ=0 EndX=114.004 EndY=-109.4 EndZ=0
    g13: LineSegment StartX=114.004 StartY=-109.4 StartZ=0 EndX=119.794 EndY=-109.4 EndZ=0
    g14: LineSegment StartX=119.794 StartY=-109.4 StartZ=0 EndX=119.794 EndY=-110.81 EndZ=0
    g15: LineSegment StartX=119.794 StartY=-110.81 StartZ=0 EndX=101.674 EndY=-110.81 EndZ=0
    g16: LineSegment StartX=101.674 StartY=-110.81 StartZ=0 EndX=101.674 EndY=-109.4 EndZ=0
    g17: LineSegment StartX=101.674 StartY=-109.4 StartZ=0 EndX=107.464 EndY=-109.4 EndZ=0
    g18: LineSegment StartX=107.464 StartY=-109.4 StartZ=0 EndX=107.464 EndY=-105.08 EndZ=0
    g19: LineSegment StartX=107.464 StartY=-105.08 StartZ=0 EndX=101.674 EndY=-105.08 EndZ=0
    g20: LineSegment StartX=101.674 StartY=-105.08 StartZ=0 EndX=101.674 EndY=-103.22 EndZ=0
    g21: LineSegment StartX=101.674 StartY=-103.22 StartZ=0 EndX=107.994 EndY=-103.22 EndZ=0
    g22: LineSegment StartX=107.994 StartY=-103.22 StartZ=0 EndX=107.994 EndY=-95.15 EndZ=0
    g23: LineSegment StartX=107.994 StartY=-95.15 StartZ=0 EndX=101.674 EndY=-95.15 EndZ=0
    g24: LineSegment StartX=101.674 StartY=-95.15 StartZ=0 EndX=101.674 EndY=-93.41 EndZ=0
    g25: LineSegment StartX=101.674 StartY=-93.41 StartZ=0 EndX=107.464 EndY=-93.41 EndZ=0
    g26: LineSegment StartX=107.464 StartY=-93.41 StartZ=0 EndX=107.464 EndY=-89.09 EndZ=0
    g27: LineSegment StartX=107.464 StartY=-89.09 StartZ=0 EndX=101.674 EndY=-89.09 EndZ=0
  constraints (84):
    c: Vertical(g0)
    c: Coincident(g0,g1)
    c: Horizontal(g1)
    c: Coincident(g1,g2)
    c: Vertical(g2)
    c: Coincident(g2,g3)
    c: Horizontal(g3)
    c: Coincident(g3,g4)
    c: Vertical(g4)
    c: Coincident(g4,g5)
    c: Horizontal(g5)
    c: Coincident(g5,g6)
    c: Vertical(g6)
    c: Coincident(g6,g7)
    c: Horizontal(g7)
    c: Coincident(g7,g8)
    c: Vertical(g8)
    c: Coincident(g8,g9)
    c: Horizontal(g9)
    c: Coincident(g9,g10)
    c: Vertical(g10)
    c: Coincident(g10,g11)
    c: Horizontal(g11)
    c: Coincident(g11,g12)
    c: Vertical(g12)
    c: Coincident(g12,g13)
    c: Horizontal(g13)
    c: Coincident(g13,g14)
    c: Vertical(g14)
    c: Coincident(g14,g15)
    c: Horizontal(g15)
    c: Coincident(g15,g16)
    c: Vertical(g16)
    c: Coincident(g16,g17)
    c: Horizontal(g17)
    c: Coincident(g17,g18)
    c: Vertical(g18)
    c: Coincident(g18,g19)
    c: Horizontal(g19)
    c: Coincident(g19,g20)
    c: Vertical(g20)
    c: Coincident(g20,g21)
    c: Horizontal(g21)
    c: Coincident(g21,g22)
    c: Vertical(g22)
    c: Coincident(g22,g23)
    c: Horizontal(g23)
    c: Coincident(g23,g24)
    c: Vertical(g24)
    c: Coincident(g24,g25)
    c: Horizontal(g25)
    c: Coincident(g25,g26)
    c: Vertical(g26)
    c: Coincident(g26,g27)
    c: Horizontal(g27)
    c: Coincident(g27,g0)
    c: DistanceX(g0) = 101.674
    c: DistanceY(g0) = -87.4
    c: DistanceY(g4,g4) = 4.32
    c: DistanceY(g2,g2) = 1.69
    c: DistanceX(g1,g1) = 18.12
    c: DistanceX(g3,g3) = 5.79
    c: Equal(g5,g3)
    c: DistanceY(g6,g6) = 1.74
    c: DistanceX(g7,g7) = 6.32
    c: DistanceY(g8,g8) = 8.07
    c: Equal(g9,g7)
    c: Equal(g11,g3)
    c: Equal(g13,g11)
    c: DistanceY(g10,g10) = 1.86
    c: DistanceY(g12,g12) = 4.32
    c: DistanceY(g14,g14) = 1.41
    c: Equal(g14,g16)
    c: DistanceX(g15,g15) = 18.12
    c: Equal(g2,g0)
    c: Equal(g26,g4)
    c: Equal(g25,g5)
    c: Equal(g24,g6)
    c: Equal(g23,g7)
    c: Equal(g27,g3)
    c: Equal(g22,g8)
    c: Equal(g21,g9)
    c: Equal(g20,g10)
    c: Equal(g19,g11)
FEATURE [PartDesign::Pad] Pad017
  Direction = (0,0,1)
  Length = 7
  Length2 = 10
  Profile = -> Sketch037
  ReferenceAxis = -> Sketch037 [N_Axis]
  Refine = true
  Suppressed = false
  Type = 0
FEATURE [PartDesign::SubShapeBinder] Binder012
  BindCopyOnChange = 0
  BindMode = 0
  ClaimChildren = false
  Context = -> Body011 [Binder012.]
  Fuse = false
  MakeFace = true
  OffsetFill = false
  OffsetIntersection = false
  OffsetJoinType = 0
  OffsetOpenResult = false
  PartialLoad = false
  Refine = true
  Relative = true
  Support = -> [watch_band_clasp001[Face2752,Face2309,Face4295]]
  _Version = 2
FEATURE [Sketcher::SketchObject] Sketch038
  ArcFitTolerance = 1e-06
  AttachmentSupport = -> [XZ_Plane014]
  ExternalGeometry = -> [Binder012]
  FullyConstrained = true
  MakeInternals = false
  MapMode = 5
  Placement = pos=(0,0,0) rot=(1,0,0;1.5708rad)
  sketch-geometry (1):
    g0: Circle CenterX=116.298 CenterY=3.50169 CenterZ=0 NormalX=0 NormalY=0 NormalZ=1 AngleXU=0 Radius=1.49435
  constraints (3):
    c: PointOnObject(g-4,g0)
    c: PointOnObject(g-3,g0)
    c: PointOnObject(g-5,g0)
FEATURE [PartDesign::Pad] Pad018
  BaseFeature = -> Pad017
  Direction = (0,-1,2e-16)
  Length = 95.9
  Length2 = -94
  Profile = -> Sketch038
  ReferenceAxis = -> Sketch038 [N_Axis]
  Refine = true
  Suppressed = false
  Type = 4
FEATURE [Sketcher::SketchObject] Sketch039
  ArcFitTolerance = 1e-06
  AttachmentSupport = -> [XZ_Plane014]
  ExternalGeometry = -> [Binder012]
  FullyConstrained = true
  MakeInternals = false
  MapMode = 5
  Placement = pos=(0,0,0) rot=(1,0,0;1.5708rad)
  sketch-geometry (1):
    g0: Circle CenterX=116.298 CenterY=3.50169 CenterZ=0 NormalX=0 NormalY=0 NormalZ=1 AngleXU=0 Radius=1.49435
  constraints (3):
    c: PointOnObject(g-5,g0)
    c: PointOnObject(g-4,g0)
    c: PointOnObject(g-3,g0)
FEATURE [PartDesign::Pad] Pad019
  BaseFeature = -> Pad018
  Direction = (0,-1,2e-16)
  Length = 102.52
  Length2 = -104
  Profile = -> Sketch039
  ReferenceAxis = -> Sketch039 [N_Axis]
  Refine = true
  Suppressed = false
  Type = 4
FEATURE [PartDesign::SubShapeBinder] Binder013
  BindCopyOnChange = 0
  BindMode = 0
  ClaimChildren = false
  Context = -> Body011 [Binder013.]
  Fuse = false
  MakeFace = true
  OffsetFill = false
  OffsetIntersection = false
  OffsetJoinType = 0
  OffsetOpenResult = false
  PartialLoad = false
  Refine = true
  Relative = true
  Support = -> [watch_band_clasp001[Face1473,Face4059,Face2840]]
  _Version = 2
FEATURE [Sketcher::SketchObject] Sketch040
  ArcFitTolerance = 1e-06
  AttachmentSupport = -> [XZ_Plane014]
  ExternalGeometry = -> [Binder013]
  FullyConstrained = true
  MakeInternals = false
  MapMode = 5
  Placement = pos=(0,0,0) rot=(1,0,0;1.5708rad)
  sketch-geometry (1):
    g0: Circle CenterX=105.17 CenterY=3.49998 CenterZ=0 NormalX=0 NormalY=0 NormalZ=1 AngleXU=0 Radius=1.49655
  constraints (3):
    c: PointOnObject(g-5,g0)
    c: PointOnObject(g-4,g0)
    c: PointOnObject(g-3,g0)
FEATURE [PartDesign::SubShapeBinder] Binder014
  BindCopyOnChange = 0
  BindMode = 0
  ClaimChildren = false
  Context = -> Body011 [Binder014.]
  Fuse = false
  MakeFace = true
  OffsetFill = false
  OffsetIntersection = false
  OffsetJoinType = 0
  OffsetOpenResult = false
  PartialLoad = false
  Refine = true
  Relative = true
  Support = -> [watch_band_clasp002[Face1473,Face4059,Face2840]]
  _Version = 2
FEATURE [Sketcher::SketchObject] Sketch041
  ArcFitTolerance = 1e-06
  AttachmentSupport = -> [XZ_Plane014]
  ExternalGeometry = -> [Binder014]
  FullyConstrained = true
  MakeInternals = false
  MapMode = 5
  Placement = pos=(0,0,0) rot=(1,0,0;1.5708rad)
  sketch-geometry (1):
    g0: Circle CenterX=105.17 CenterY=3.49998 CenterZ=0 NormalX=0 NormalY=0 NormalZ=1 AngleXU=0 Radius=1.49655
  constraints (3):
    c: PointOnObject(g-5,g0)
    c: PointOnObject(g-4,g0)
    c: PointOnObject(g-3,g0)
FEATURE [Part::Feature] watch_band_clasp002
  shape: bbox 18.13 x 23.41 x 7 mm, 4570 faces, 0 solids (baked)
FEATURE [PartDesign::Pad] Pad020
  BaseFeature = -> Pad019
  Direction = (0,-1,2e-16)
  Length = 95.9
  Length2 = -94
  Profile = -> Sketch040
  ReferenceAxis = -> Sketch040 [N_Axis]
  Refine = true
  Suppressed = false
  Type = 4
FEATURE [PartDesign::Pad] Pad021
  BaseFeature = -> Pad020
  Direction = (0,-1,2e-16)
  Length = 102.52
  Length2 = -104
  Profile = -> Sketch041
  ReferenceAxis = -> Sketch041 [N_Axis]
  Refine = true
  Suppressed = false
  Type = 4
FEATURE [Sketcher::SketchObject] Sketch042
  ArcFitTolerance = 1e-06
  AttachmentSupport = -> [XZ_Plane014]
  FullyConstrained = true
  MakeInternals = false
  MapMode = 5
  Placement = pos=(0,0,0) rot=(1,0,0;1.5708rad)
  sketch-geometry (4):
    g0: LineSegment StartX=109.294 StartY=-1 StartZ=0 EndX=120.794 EndY=-1 EndZ=0
    g1: LineSegment StartX=120.794 StartY=-1 StartZ=0 EndX=120.794 EndY=8 EndZ=0
    g2: LineSegment StartX=120.794 StartY=8 StartZ=0 EndX=112.57 EndY=8 EndZ=0
    g3: LineSegment StartX=112.57 StartY=8 StartZ=0 EndX=109.294 EndY=-1 EndZ=0
  constraints (12):
    c: Horizontal(g0)
    c: Coincident(g0,g1)
    c: Vertical(g1)
    c: Coincident(g1,g2)
    c: Horizontal(g2)
    c: Coincident(g2,g3)
    c: Coincident(g3,g0)
    c: Angle(g0,g3) = 1.22173
    c: DistanceY(g0) = -1
    c: DistanceY(g1,g1) = 9
    c: DistanceX(g-3,g0) = 1
    c: DistanceX(g0,g0) = 11.5
FEATURE [Mesh::Feature] watch_band_regular_link  label="watch-band-regular-link"
FEATURE [Part::Feature] watch_band_regular_link001
  Placement = pos=(-7,0,0) rot=(0,0,1;0rad)
  shape: bbox 17.06 x 23.9 x 7 mm, 1518 faces, 0 solids (baked)
FEATURE [PartDesign::Fillet] Fillet005
  Base = -> Pad021 [Edge96,Edge94,Edge90,Edge92]
  BaseFeature = -> Pad021
  Radius = 0.7
  Refine = true
  SupportTransform = false
  Suppressed = false
  UseAllEdges = false
FEATURE [PartDesign::Pocket] Pocket016
  BaseFeature = -> Fillet005
  Direction = (0,1,-2e-16)
  Length = 200
  Length2 = 5
  Profile = -> Sketch042
  ReferenceAxis = -> Sketch042 [N_Axis]
  Refine = true
  Reversed = true
  Suppressed = false
  Type = 0
FEATURE [PartDesign::Fillet] Fillet006
  Base = -> Pocket016 [Edge9,Edge5,Edge27,Edge35,Edge13,Edge45,Edge19,Edge1]
  BaseFeature = -> Pocket016
  Radius = 2
  Refine = true
  SupportTransform = false
  Suppressed = false
  UseAllEdges = false
FEATURE [PartDesign::Body] Body011
  AllowCompound = false
  Group = -> [Sketch037,Pad017,Binder012,Sketch038,Pad018,Sketch039,Pad019,Binder013,Sketch040,Sketch041,Binder014,Pad020,Pad021,Sketch042,Fillet005,Pocket016,Fillet006]
  Origin = -> Origin014
  Tip = -> Fillet006
FEATURE [PartDesign::FeatureBase] Clone004
  BaseFeature = -> Body011
  Placement = pos=(-112.21,87.4,-7) rot=(0,0,1;0rad)
  Suppressed = false
FEATURE [PartDesign::Body] Body012  label="strap-holder"
  AllowCompound = false
  Group = -> [Clone004]
  Origin = -> Origin015
  Placement = pos=(-22.9469,-33,6.56173) rot=(0,1,0;5.93412rad)
  Tip = -> Clone004
FEATURE [PartDesign::FeatureBase] Clone005
  BaseFeature = -> Body012
  Placement = pos=(-22.9469,-33,6.56173) rot=(0,1,0;5.93412rad)
  Suppressed = false
FEATURE [PartDesign::Body] Body013
  AllowCompound = false
  Group = -> [Clone005]
  Origin = -> Origin016
  Tip = -> Clone005
FEATURE [Part::Mirroring] Part__Mirroring  label="Body013 (Mirror #1)"
  Base = (0,0,0)
  Normal = (1,0,0)
  Placement = pos=(0.4,0,0) rot=(0,0,1;0rad)
  Source = -> Body013
FEATURE [PartDesign::FeatureBase] Clone006
  BaseFeature = -> Body010
  Placement = pos=(0,-57.7,0) rot=(0,0,1;0rad)
  Suppressed = false
FEATURE [PartDesign::Body] Body014  label="cage-final"
  AllowCompound = false
  Group = -> [Clone006]
  Origin = -> Origin017
  Placement = pos=(0,-57.6,0) rot=(0,0,1;0rad)
  Tip = -> Clone006
FEATURE [Part::MultiFuse] Fusion
  Shapes = -> [Body012,Part__Mirroring,Body014]
FEATURE [PartDesign::FeatureBase] BaseFeature
  BaseFeature = -> Fusion
  Suppressed = false
FEATURE [Sketcher::SketchObject] Sketch043
  ArcFitTolerance = 1e-06
  AttachmentSupport = -> [XZ_Plane018]
  ExternalGeometry = -> [BaseFeature]
  FullyConstrained = false
  MakeInternals = false
  MapMode = 5
  Placement = pos=(0,0,0) rot=(1,0,0;1.5708rad)
  sketch-geometry (4):
    g0: LineSegment StartX=-32.965 StartY=-1.9 StartZ=0 EndX=-32.965 EndY=-18.4013 EndZ=0
    g1: LineSegment StartX=-32.965 StartY=-18.4013 StartZ=0 EndX=33.365 EndY=-18.4013 EndZ=0
    g2: LineSegment StartX=33.365 StartY=-18.4013 StartZ=0 EndX=33.365 EndY=-1.9 EndZ=0
    g3: LineSegment StartX=33.365 StartY=-1.9 StartZ=0 EndX=-32.965 EndY=-1.9 EndZ=0
  constraints (11):
    c: Coincident(g0,g1)
    c: Coincident(g1,g2)
    c: Coincident(g2,g3)
    c: Coincident(g3,g0)
    c: Vertical(g0)
    c: Vertical(g2)
    c: Horizontal(g1)
    c: Horizontal(g3)
    c: DistanceY(g2,g-3) = 0
    c: DistanceX(g-3,g2) = 10
    c: DistanceX(g0,g-3) = 10
FEATURE [PartDesign::Pocket] Pocket017
  BaseFeature = -> BaseFeature
  Direction = (0,1,-2e-16)
  Length = 200
  Length2 = 5
  Profile = -> Sketch043
  ReferenceAxis = -> Sketch043 [N_Axis]
  Refine = true
  Reversed = true
  Suppressed = false
  Type = 0
FEATURE [Sketcher::SketchObject] Sketch044
  ArcFitTolerance = 1e-06
  AttachmentSupport = -> [XY_Plane018]
  ExternalGeometry = -> [Pocket017]
  FullyConstrained = true
  MakeInternals = false
  MapMode = 5
  sketch-geometry (4):
    g0: LineSegment StartX=6.265 StartY=-25.215 StartZ=0 EndX=6.265 EndY=-29.765 EndZ=0
    g1: LineSegment StartX=6.265 StartY=-29.765 StartZ=0 EndX=10.265 EndY=-29.765 EndZ=0
    g2: LineSegment StartX=10.265 StartY=-29.765 StartZ=0 EndX=10.265 EndY=-25.215 EndZ=0
    g3: LineSegment StartX=10.265 StartY=-25.215 StartZ=0 EndX=6.265 EndY=-25.215 EndZ=0
  constraints (12):
    c: Coincident(g0,g1)
    c: Coincident(g1,g2)
    c: Coincident(g2,g3)
    c: Coincident(g3,g0)
    c: Vertical(g0)
    c: Vertical(g2)
    c: Horizontal(g1)
    c: Horizontal(g3)
    c: Vertical(g-3,g0)
    c: Vertical(g-4,g1)
    c: DistanceY(g-3,g0) = 0
    c: DistanceY(g1,g-4) = 0
FEATURE [PartDesign::Pocket] Pocket018
  BaseFeature = -> Pocket017
  Direction = (0,0,-1)
  Length = 20
  Length2 = 5
  Profile = -> Sketch044
  ReferenceAxis = -> Sketch044 [N_Axis]
  Refine = true
  Reversed = true
  Suppressed = false
  Type = 0
FEATURE [Sketcher::SketchObject] Sketch045
  ArcFitTolerance = 1e-06
  AttachmentSupport = -> [XY_Plane018]
  ExternalGeometry = -> [Pocket018]
  FullyConstrained = true
  MakeInternals = false
  MapMode = 5
  sketch-geometry (4):
    g0: LineSegment StartX=-13.865 StartY=-35.215 StartZ=0 EndX=14.265 EndY=-35.215 EndZ=0
    g1: LineSegment StartX=14.265 StartY=-35.215 StartZ=0 EndX=14.265 EndY=-25.215 EndZ=0
    g2: LineSegment StartX=14.265 StartY=-25.215 StartZ=0 EndX=-13.865 EndY=-25.215 EndZ=0
    g3: LineSegment StartX=-13.865 StartY=-25.215 StartZ=0 EndX=-13.865 EndY=-35.215 EndZ=0
  constraints (12):
    c: Coincident(g0,g1)
    c: Coincident(g1,g2)
    c: Coincident(g2,g3)
    c: Coincident(g3,g0)
    c: Horizontal(g0)
    c: Horizontal(g2)
    c: Vertical(g1)
    c: Vertical(g3)
    c: DistanceX(g-4,g0) = -2.3
    c: DistanceX(g-3,g0) = 4.55
    c: DistanceY(g-3,g0) = 0
    c: DistanceY(g-5,g1) = 0
FEATURE [PartDesign::Pad] Pad022
  BaseFeature = -> Pocket018
  Direction = (0,0,1)
  Length = 1.9
  Length2 = -0.1
  Profile = -> Sketch045
  ReferenceAxis = -> Sketch045 [N_Axis]
  Refine = true
  Reversed = true
  Suppressed = false
  Type = 4
FEATURE [Sketcher::SketchObject] Sketch046
  ArcFitTolerance = 1e-06
  AttachmentSupport = -> [XY_Plane018]
  ExternalGeometry = -> [Pad022]
  FullyConstrained = true
  MakeInternals = false
  MapMode = 5
  sketch-geometry (4):
    g0: LineSegment StartX=-13.865 StartY=-25.215 StartZ=0 EndX=-13.865 EndY=-27.115 EndZ=0
    g1: LineSegment StartX=-13.865 StartY=-27.115 StartZ=0 EndX=14.265 EndY=-27.115 EndZ=0
    g2: LineSegment StartX=14.265 StartY=-27.115 StartZ=0 EndX=14.265 EndY=-25.215 EndZ=0
    g3: LineSegment StartX=14.265 StartY=-25.215 StartZ=0 EndX=-13.865 EndY=-25.215 EndZ=0
  constraints (12):
    c: Coincident(g0,g1)
    c: Coincident(g1,g2)
    c: Coincident(g2,g3)
    c: Coincident(g3,g0)
    c: Vertical(g0)
    c: Vertical(g2)
    c: Horizontal(g1)
    c: Horizontal(g3)
    c: DistanceY(g1,g-3) = 0
    c: DistanceY(g-4,g2) = 0
    c: DistanceX(g-6,g2) = 0
    c: DistanceX(g0,g-5) = 0
FEATURE [PartDesign::Pad] Pad023
  BaseFeature = -> Pad022
  Direction = (0,0,1)
  Length = 2
  Length2 = 1
  Profile = -> Sketch046
  ReferenceAxis = -> Sketch046 [N_Axis]
  Refine = true
  Suppressed = false
  Type = 4
FEATURE [PartDesign::Fillet] Fillet
  Base = -> Pad023 [Edge347,Edge344]
  BaseFeature = -> Pad023
  Radius = 2
  Refine = true
  SupportTransform = false
  Suppressed = false
  UseAllEdges = false
FEATURE [PartDesign::Chamfer] Chamfer001
  Angle = 45
  Base = -> Fillet [Edge53,Edge51,Edge47,Edge57]
  BaseFeature = -> Fillet
  ChamferType = 0
  FlipDirection = false
  Refine = true
  Size = 1
  Size2 = 1
  SupportTransform = false
  Suppressed = false
  UseAllEdges = false
FEATURE [PartDesign::Fillet] Fillet007
  Base = -> Chamfer001 [Edge110,Edge295,Edge288,Edge292]
  BaseFeature = -> Chamfer001
  Radius = 1
  Refine = true
  SupportTransform = false
  Suppressed = false
  UseAllEdges = false
FEATURE [PartDesign::Fillet] Fillet008
  Base = -> Fillet007 [Edge23,Edge258,Edge303,Edge202]
  BaseFeature = -> Fillet007
  Radius = 1
  Refine = true
  SupportTransform = false
  Suppressed = false
  UseAllEdges = false
FEATURE [Sketcher::SketchObject] Sketch047
  ArcFitTolerance = 1e-06
  AttachmentSupport = -> [XY_Plane018]
  ExternalGeometry = -> [Fillet008]
  FullyConstrained = true
  MakeInternals = false
  MapMode = 5
  sketch-geometry (4):
    g0: LineSegment StartX=-9.86499 StartY=-35.215 StartZ=0 EndX=10.265 EndY=-35.215 EndZ=0
    g1: LineSegment StartX=10.265 StartY=-35.215 StartZ=0 EndX=10.265 EndY=-29.215 EndZ=0
    g2: LineSegment StartX=10.265 StartY=-29.215 StartZ=0 EndX=-9.86499 EndY=-29.215 EndZ=0
    g3: LineSegment StartX=-9.86499 StartY=-29.215 StartZ=0 EndX=-9.86499 EndY=-35.215 EndZ=0
  constraints (12):
    c: Coincident(g0,g1)
    c: Coincident(g1,g2)
    c: Coincident(g2,g3)
    c: Coincident(g3,g0)
    c: Horizontal(g0)
    c: Horizontal(g2)
    c: Vertical(g1)
    c: Vertical(g3)
    c: DistanceY(g1,g-7) = 4
    c: DistanceY(g-6,g0) = 4
    c: DistanceX(g0,g-5) = 4
    c: DistanceX(g-3,g0) = 4
FEATURE [PartDesign::Pocket] Pocket019
  BaseFeature = -> Fillet008
  Direction = (0,0,-1)
  Length = 5
  Length2 = 5
  Profile = -> Sketch047
  ReferenceAxis = -> Sketch047 [N_Axis]
  Refine = true
  Suppressed = false
  Type = 0
FEATURE [PartDesign::Fillet] Fillet009
  Base = -> Pocket019 [Edge265,Edge266,Edge267,Edge263]
  BaseFeature = -> Pocket019
  Radius = 1
  Refine = true
  SupportTransform = false
  Suppressed = false
  UseAllEdges = false
FEATURE [PartDesign::Fillet] Fillet010
  Base = -> Fillet009 [Edge82,Edge52,Edge151,Edge80]
  BaseFeature = -> Fillet009
  Radius = 1
  Refine = true
  SupportTransform = false
  Suppressed = false
  UseAllEdges = false
FEATURE [PartDesign::Fillet] Fillet011
  Base = -> Fillet010 [Edge172,Edge188,Edge169,Edge186]
  BaseFeature = -> Fillet010
  Radius = 1
  Refine = true
  SupportTransform = false
  Suppressed = false
  UseAllEdges = false
FEATURE [Sketcher::SketchObject] Sketch048
  ArcFitTolerance = 1e-06
  AttachmentSupport = -> [XY_Plane018]
  ExternalGeometry = -> [Fillet011]
  FullyConstrained = false
  MakeInternals = false
  MapMode = 5
  sketch-geometry (16):
    g0: LineSegment StartX=-36.2134 StartY=-32.215 StartZ=0 EndX=-36.2134 EndY=-35.215 EndZ=0
    g1: LineSegment StartX=-36.2134 StartY=-35.215 StartZ=0 EndX=-22.9509 EndY=-35.215 EndZ=0
    g2: LineSegment StartX=-22.9509 StartY=-35.215 StartZ=0 EndX=-22.9509 EndY=-32.215 EndZ=0
    g3: LineSegment StartX=-22.9509 StartY=-32.215 StartZ=0 EndX=-36.2134 EndY=-32.215 EndZ=0
    g4: LineSegment StartX=23.3509 StartY=-32.215 StartZ=0 EndX=23.3509 EndY=-35.215 EndZ=0
    g5: LineSegment StartX=23.3509 StartY=-35.215 StartZ=0 EndX=38.2786 EndY=-35.215 EndZ=0
    g6: LineSegment StartX=38.2786 StartY=-35.215 StartZ=0 EndX=38.2786 EndY=-32.215 EndZ=0
    g7: LineSegment StartX=38.2786 StartY=-32.215 StartZ=0 EndX=23.3509 EndY=-32.215 EndZ=0
    g8: LineSegment StartX=23.3509 StartY=-57.4946 StartZ=0 EndX=38.2786 EndY=-57.4946 EndZ=0
    g9: LineSegment StartX=38.2786 StartY=-57.4946 StartZ=0 EndX=38.2786 EndY=-54.185 EndZ=0
    g10: LineSegment StartX=38.2786 StartY=-54.185 StartZ=0 EndX=23.3509 EndY=-54.185 EndZ=0
    g11: LineSegment StartX=23.3509 StartY=-54.185 StartZ=0 EndX=23.3509 EndY=-57.4946 EndZ=0
    g12: LineSegment StartX=-22.9509 StartY=-56.8976 StartZ=0 EndX=-22.9509 EndY=-54.185 EndZ=0
    g13: LineSegment StartX=-22.9509 StartY=-54.185 StartZ=0 EndX=-36.2134 EndY=-54.185 EndZ=0
    g14: LineSegment StartX=-36.2134 StartY=-54.185 StartZ=0 EndX=-36.2134 EndY=-56.8976 EndZ=0
    g15: LineSegment StartX=-36.2134 StartY=-56.8976 StartZ=0 EndX=-22.9509 EndY=-56.8976 EndZ=0
  constraints (44):
    c: Coincident(g0,g1)
    c: Coincident(g1,g2)
    c: Coincident(g2,g3)
    c: Coincident(g3,g0)
    c: Vertical(g0)
    c: Vertical(g2)
    c: Horizontal(g1)
    c: Horizontal(g3)
    c: Coincident(g4,g5)
    c: Coincident(g5,g6)
    c: Coincident(g6,g7)
    c: Coincident(g7,g4)
    c: Vertical(g4)
    c: Vertical(g6)
    c: Horizontal(g5)
    c: Horizontal(g7)
    c: Coincident(g8,g9)
    c: Coincident(g9,g10)
    c: Coincident(g10,g11)
    c: Coincident(g11,g8)
    c: Horizontal(g8)
    c: Horizontal(g10)
    c: Vertical(g9)
    c: Vertical(g11)
    c: Coincident(g12,g13)
    c: Coincident(g13,g14)
    c: Coincident(g14,g15)
    c: Coincident(g15,g12)
    c: Vertical(g12)
    c: Vertical(g14)
    c: Horizontal(g13)
    c: Horizontal(g15)
    c: DistanceY(g-4,g1) = 0
    c: DistanceY(g-4,g4) = 0
    c: DistanceY(g-3,g10) = 0
    c: DistanceY(g-3,g12) = 0
    c: DistanceX(g12,g1) = 0
    c: DistanceX(g10,g4) = 0
    c: DistanceX(g13,g0) = 0
    c: DistanceX(g5,g9) = 0
    c: DistanceY(g6,g6) = 3
    c: DistanceX(g4,g-6) = 0
    c: DistanceX(g-5,g2) = 0
    c: Equal(g0,g6)
FEATURE [PartDesign::Pocket] Pocket020
  BaseFeature = -> Fillet011
  Direction = (0,0,-1)
  Length = 8
  Length2 = 5
  Profile = -> Sketch048
  ReferenceAxis = -> Sketch048 [N_Axis]
  Refine = true
  Reversed = true
  Suppressed = false
  Type = 4
FEATURE [PartDesign::Fillet] Fillet012
  Base = -> Pocket020 [Edge336,Edge335,Edge308,Edge307]
  BaseFeature = -> Pocket020
  Radius = 1.2
  Refine = true
  SupportTransform = false
  Suppressed = false
  UseAllEdges = false
FEATURE [PartDesign::Fillet] Fillet013
  Base = -> Fillet012 [Edge226,Edge222,Edge230,Edge29,Edge25,Edge23]
  BaseFeature = -> Fillet012
  Radius = 1
  Refine = true
  SupportTransform = false
  Suppressed = false
  UseAllEdges = false
FEATURE [PartDesign::Fillet] Fillet014
  Base = -> Fillet013 [Edge27,Edge11,Edge180,Edge165]
  BaseFeature = -> Fillet013
  Radius = 1
  Refine = true
  SupportTransform = false
  Suppressed = false
  UseAllEdges = false
FEATURE [PartDesign::Fillet] Fillet015
  Base = -> Fillet014 [Edge107,Edge305]
  BaseFeature = -> Fillet014
  Radius = 1
  Refine = true
  SupportTransform = false
  Suppressed = false
  UseAllEdges = false
FEATURE [PartDesign::Body] Body015  label="strap-holder001"
  AllowCompound = false
  BaseFeature = -> Fusion
  Group = -> [BaseFeature,Sketch043,Pocket017,Sketch044,Pocket018,Sketch045,Pad022,Sketch046,Pad023,Fillet,Chamfer001,Fillet007,Fillet008,Sketch047,Pocket019,Fillet009,Fillet010,Fillet011,Sketch048,Pocket020,Fillet012,Fillet013,Fillet014,Fillet015]
  Origin = -> Origin018
  Placement = pos=(0,57.6,0) rot=(0,0,1;0rad)
  Tip = -> Fillet015
